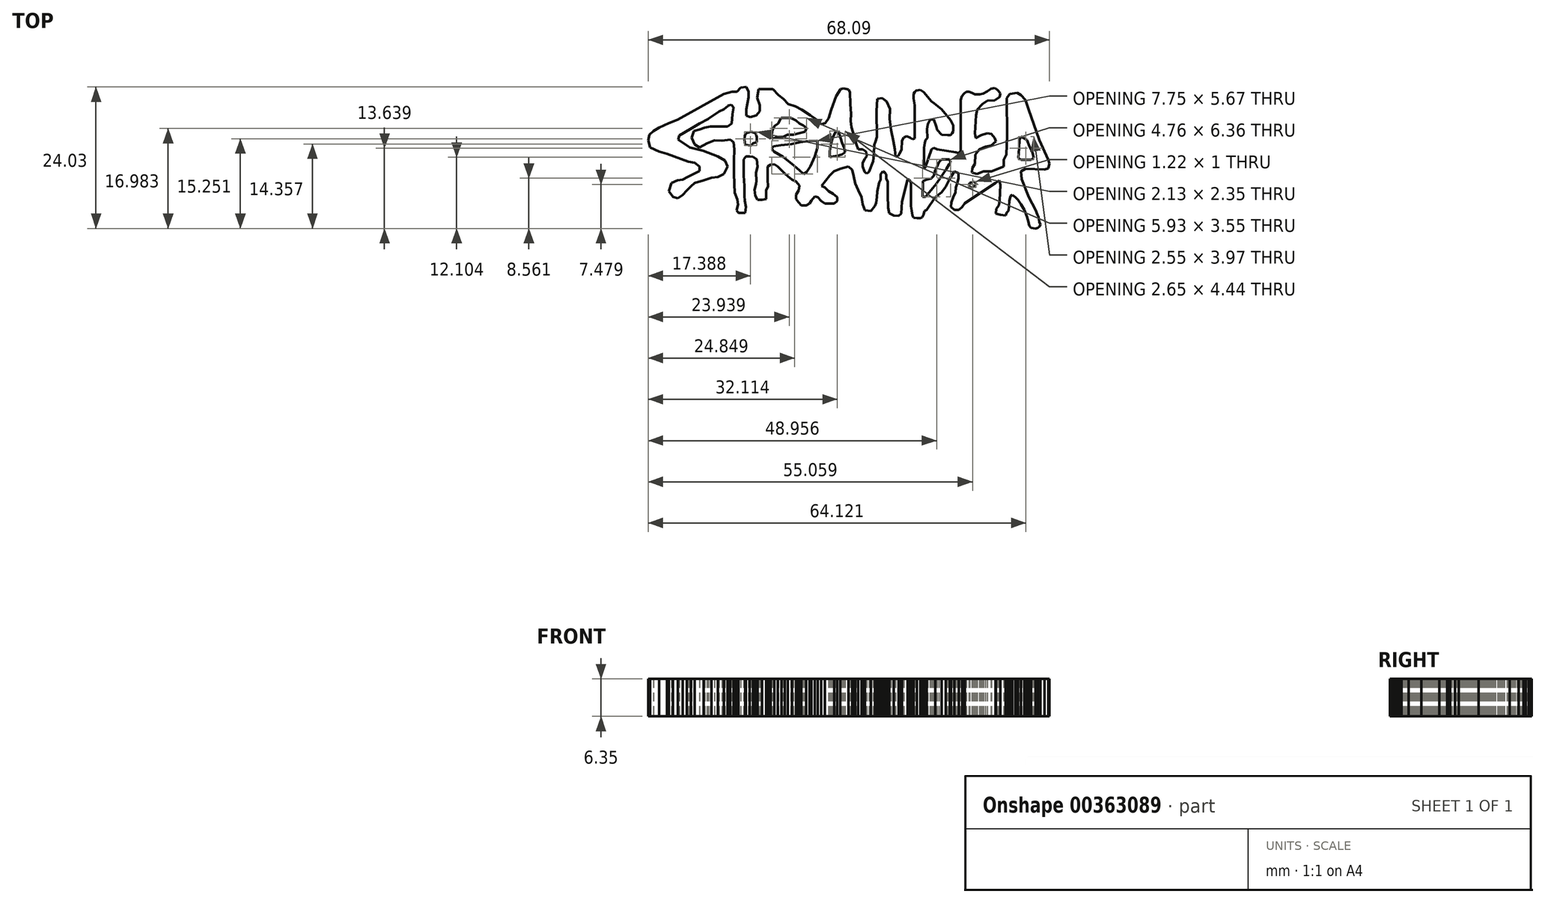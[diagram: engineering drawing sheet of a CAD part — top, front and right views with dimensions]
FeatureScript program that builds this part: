
annotation { "Feature Type Name" : "Feature", "Feature Type Description" : "" }
export const myFeature = defineFeature(function(context is Context, id is Id, definition is map)
    precondition{}
    {
        {
            var Q0;
            Q0=qCreatedBy(makeId("Top.planeOp"),FACE);
            var sketch = newSketch(context, id + "F0", { "sketchPlane" : qUnion([Q0])});
            skPoint(sketch, "E0", {"position": v(-28.93, -5.4) * mm});
            skPoint(sketch, "E1", {"position": v(-28.86, 4.62) * mm});
            skPoint(sketch, "E2", {"position": v(-19.82, 7.3) * mm});
            skPoint(sketch, "E3", {"position": v(-26.2, 6.07) * mm});
            skPoint(sketch, "E4", {"position": v(-26.62, 4.93) * mm});
            skPoint(sketch, "E5", {"position": v(-26.09, 3.8) * mm});
            skPoint(sketch, "E6", {"position": v(-25.23, 3.26) * mm});
            skPoint(sketch, "E7", {"position": v(-24.01, 3.96) * mm});
            skPoint(sketch, "E8", {"position": v(-22.75, 4.49) * mm});
            skPoint(sketch, "E9", {"position": v(-21.45, 4.4) * mm});
            skPoint(sketch, "E10", {"position": v(-20.02, 4.57) * mm});
            skPoint(sketch, "E11", {"position": v(-20.51, 0) * mm});
            skPoint(sketch, "E12", {"position": v(-20.92, 1.03) * mm});
            skPoint(sketch, "E13", {"position": v(-22.14, 1.76) * mm});
            skPoint(sketch, "E14", {"position": v(-24.62, 2.7) * mm});
            skPoint(sketch, "E15", {"position": v(-26.9, 3.26) * mm});
            skPoint(sketch, "E16", {"position": v(-26.82, 6.4) * mm});
            skPoint(sketch, "E17", {"position": v(-23.77, 8.1) * mm});
            skPoint(sketch, "E18", {"position": v(-21.94, 9.33) * mm});
            skPoint(sketch, "E19", {"position": v(-25.23, 7.33) * mm});
            skPoint(sketch, "E20", {"position": v(-28.12, -4.83) * mm});
            skPoint(sketch, "E21", {"position": v(-27.39, -4.02) * mm});
            skPoint(sketch, "E22", {"position": v(-26.74, -3.33) * mm});
            skPoint(sketch, "E23", {"position": v(-26.09, -2.76) * mm});
            skPoint(sketch, "E24", {"position": v(-24.54, -2.35) * mm});
            skPoint(sketch, "E25", {"position": v(-23.24, -1.9) * mm});
            skPoint(sketch, "E26", {"position": v(-22.14, -1.74) * mm});
            skPoint(sketch, "E27", {"position": v(-21.12, -1.25) * mm});
            skPoint(sketch, "E28", {"position": v(-29.79, -5.12) * mm});
            skPoint(sketch, "E29", {"position": v(-30.44, -4.18) * mm});
            skPoint(sketch, "E30", {"position": v(-30.03, -2.76) * mm});
            skPoint(sketch, "E31", {"position": v(-28.98, -2.31) * mm});
            skPoint(sketch, "E32", {"position": v(-28.12, -2.19) * mm});
            skPoint(sketch, "E33", {"position": v(-27.3, -1.74) * mm});
            skPoint(sketch, "E34", {"position": v(-26.09, -1.25) * mm});
            skPoint(sketch, "E35", {"position": v(-25.23, -0.76) * mm});
            skPoint(sketch, "E36", {"position": v(-25.23, 0) * mm});
            skPoint(sketch, "E37", {"position": v(-26.09, 0.66) * mm});
            skPoint(sketch, "E38", {"position": v(-27.18, 0.86) * mm});
            skPoint(sketch, "E39", {"position": v(-30.77, 2.17) * mm});
            skPoint(sketch, "E40", {"position": v(-32.1, 2.53) * mm});
            skPoint(sketch, "E41", {"position": v(-33.61, 3.26) * mm});
            skPoint(sketch, "E42", {"position": v(-33.98, 4.49) * mm});
            skPoint(sketch, "E43", {"position": v(-33.78, 5.42) * mm});
            skPoint(sketch, "E44", {"position": v(-21.12, 9.73) * mm});
            skPoint(sketch, "E45", {"position": v(-33.04, 6.07) * mm});
            skPoint(sketch, "E46", {"position": v(-32.1, 6.64) * mm});
            skPoint(sketch, "E47", {"position": v(-30.44, 7.37) * mm});
            skPoint(sketch, "E48", {"position": v(-29.02, 7.98) * mm});
            skPoint(sketch, "E49", {"position": v(-21.12, 12.34) * mm});
            skPoint(sketch, "E50", {"position": v(-19.74, 12.75) * mm});
            skPoint(sketch, "E51", {"position": v(-18.88, 12.75) * mm});
            skPoint(sketch, "E52", {"position": v(-18.27, 13.4) * mm});
            skPoint(sketch, "E53", {"position": v(-17.3, 13.52) * mm});
            skPoint(sketch, "E54", {"position": v(-16.97, 12.75) * mm});
            skPoint(sketch, "E55", {"position": v(-16.97, 11.77) * mm});
            skPoint(sketch, "E56", {"position": v(-17.3, 9.73) * mm});
            skPoint(sketch, "E57", {"position": v(-17.3, 8.68) * mm});
            skPoint(sketch, "E58", {"position": v(-16.6, 8.4) * mm});
            skPoint(sketch, "E59", {"position": v(-15.59, 8.72) * mm});
            skPoint(sketch, "E60", {"position": v(-15.02, 9.4) * mm});
            skPoint(sketch, "E61", {"position": v(-15.06, 10.43) * mm});
            skPoint(sketch, "E62", {"position": v(-15.5, 11.73) * mm});
            skPoint(sketch, "E63", {"position": v(-15.2, 13.17) * mm});
            skPoint(sketch, "E64", {"position": v(-12.8, 13.17) * mm});
            skPoint(sketch, "E65", {"position": v(-11.84, 12.14) * mm});
            skPoint(sketch, "E66", {"position": v(-11.03, 11.48) * mm});
            skPoint(sketch, "E67", {"position": v(-10.22, 10.63) * mm});
            skPoint(sketch, "E68", {"position": v(-9, 10.22) * mm});
            skPoint(sketch, "E69", {"position": v(-7.9, 9.65) * mm});
            skPoint(sketch, "E70", {"position": v(-6.47, 8.72) * mm});
            skPoint(sketch, "E71", {"position": v(-5.25, 7.9) * mm});
            skPoint(sketch, "E72", {"position": v(-4.64, 7.17) * mm});
            skPoint(sketch, "E73", {"position": v(-3.95, 7.37) * mm});
            skPoint(sketch, "E74", {"position": v(-3.38, 8.19) * mm});
            skPoint(sketch, "E75", {"position": v(-2.9, 9.65) * mm});
            skPoint(sketch, "E76", {"position": v(-2.08, 11.97) * mm});
            skPoint(sketch, "E77", {"position": v(-1.34, 13.17) * mm});
            skPoint(sketch, "E78", {"position": v(-24.38, 6.6) * mm});
            skPoint(sketch, "E79", {"position": v(-23.4, 6.8) * mm});
            skPoint(sketch, "E80", {"position": v(-22.26, 6.8) * mm});
            skPoint(sketch, "E81", {"position": v(-21.45, 6.8) * mm});
            skPoint(sketch, "E82", {"position": v(-20.47, 6.8) * mm});
            skPoint(sketch, "E83", {"position": v(-19.66, 8.88) * mm});
            skPoint(sketch, "E84", {"position": v(-17.66, 4.57) * mm});
            skPoint(sketch, "E85", {"position": v(-17.58, 5.25) * mm});
            skPoint(sketch, "E86", {"position": v(-17.4, 5.7) * mm});
            skPoint(sketch, "E87", {"position": v(-16.52, 5.92) * mm});
            skPoint(sketch, "E88", {"position": v(-25.23, 6.33) * mm});
            skPoint(sketch, "E89", {"position": v(-15.72, 5.7) * mm});
            skPoint(sketch, "E90", {"position": v(-15.53, 5) * mm});
            skPoint(sketch, "E91", {"position": v(-15.53, 4.17) * mm});
            skPoint(sketch, "E92", {"position": v(-16.2, 3.92) * mm});
            skPoint(sketch, "E93", {"position": v(-16.52, 3.56) * mm});
            skPoint(sketch, "E94", {"position": v(-17.52, 3.73) * mm});
            skPoint(sketch, "E95", {"position": v(-11.95, 7.33) * mm});
            skPoint(sketch, "E96", {"position": v(-12.56, 6.89) * mm});
            skPoint(sketch, "E97", {"position": v(-12.9, 6.17) * mm});
            skPoint(sketch, "E98", {"position": v(-13, 5.4) * mm});
            skPoint(sketch, "E99", {"position": v(-13, 4.7) * mm});
            skPoint(sketch, "E100", {"position": v(-11.95, 5) * mm});
            skPoint(sketch, "E101", {"position": v(-11.1, 5) * mm});
            skPoint(sketch, "E102", {"position": v(-10.32, 5.4) * mm});
            skPoint(sketch, "E103", {"position": v(-9.3, 5.4) * mm});
            skPoint(sketch, "E104", {"position": v(-8.35, 5.7) * mm});
            skPoint(sketch, "E105", {"position": v(-7.33, 5.92) * mm});
            skPoint(sketch, "E106", {"position": v(-7.08, 6.53) * mm});
            skPoint(sketch, "E107", {"position": v(-7.69, 7) * mm});
            skPoint(sketch, "E108", {"position": v(-8.32, 7.33) * mm});
            skPoint(sketch, "E109", {"position": v(-8.85, 7.8) * mm});
            skPoint(sketch, "E110", {"position": v(-11.4, 8.25) * mm});
            skPoint(sketch, "E111", {"position": v(-9.8, 8.25) * mm});
            skPoint(sketch, "E112", {"position": v(-19.45, 4.15) * mm});
            skPoint(sketch, "E113", {"position": v(-19.33, 2.97) * mm});
            skPoint(sketch, "E114", {"position": v(-19.41, 1.04) * mm});
            skPoint(sketch, "E115", {"position": v(-19.41, -1.12) * mm});
            skPoint(sketch, "E116", {"position": v(-19.33, -2.96) * mm});
            skPoint(sketch, "E117", {"position": v(-19.29, -4.43) * mm});
            skPoint(sketch, "E118", {"position": v(-18.84, -5.58) * mm});
            skPoint(sketch, "E119", {"position": v(-18.72, -6.44) * mm});
            skPoint(sketch, "E120", {"position": v(-18.96, -7.42) * mm});
            skPoint(sketch, "E121", {"position": v(-18.63, -7.87) * mm});
            skPoint(sketch, "E122", {"position": v(-17.53, -7.83) * mm});
            skPoint(sketch, "E123", {"position": v(-17.4, -6.85) * mm});
            skPoint(sketch, "E124", {"position": v(-17.57, -5.82) * mm});
            skPoint(sketch, "E125", {"position": v(-17.65, -4.93) * mm});
            skPoint(sketch, "E126", {"position": v(-17.61, -3.29) * mm});
            skPoint(sketch, "E127", {"position": v(-17.73, -1.53) * mm});
            skPoint(sketch, "E128", {"position": v(-17.73, 0) * mm});
            skPoint(sketch, "E129", {"position": v(-17.73, 1.25) * mm});
            skPoint(sketch, "E130", {"position": v(-17.4, 1.74) * mm});
            skPoint(sketch, "E131", {"position": v(-16.18, 1.66) * mm});
            skPoint(sketch, "E132", {"position": v(-15.53, 1.25) * mm});
            skPoint(sketch, "E133", {"position": v(-16.75, 1.74) * mm});
            skPoint(sketch, "E134", {"position": v(-15.44, 0) * mm});
            skPoint(sketch, "E135", {"position": v(-15.69, -1.04) * mm});
            skPoint(sketch, "E136", {"position": v(-15.6, -2.4) * mm});
            skPoint(sketch, "E137", {"position": v(-15.69, -2.96) * mm});
            skPoint(sketch, "E138", {"position": v(-15.4, -5.62) * mm});
            skPoint(sketch, "E139", {"position": v(-15.94, -3.94) * mm});
            skPoint(sketch, "E140", {"position": v(-15.81, -4.97) * mm});
            skPoint(sketch, "E141", {"position": v(-14.63, -5.66) * mm});
            skPoint(sketch, "E142", {"position": v(-13.97, -4.97) * mm});
            skPoint(sketch, "E143", {"position": v(-13.97, -5.5) * mm});
            skPoint(sketch, "E144", {"position": v(-13.97, -4.03) * mm});
            skPoint(sketch, "E145", {"position": v(-13.65, -3.33) * mm});
            skPoint(sketch, "E146", {"position": v(-13.69, -2.19) * mm});
            skPoint(sketch, "E147", {"position": v(-13.69, -0.96) * mm});
            skPoint(sketch, "E148", {"position": v(-13.69, 0) * mm});
            skPoint(sketch, "E149", {"position": v(-13.2, 0.35) * mm});
            skPoint(sketch, "E150", {"position": v(-12.54, 0.4) * mm});
            skPoint(sketch, "E151", {"position": v(-11.97, 0) * mm});
            skPoint(sketch, "E152", {"position": v(-11.36, -0.63) * mm});
            skPoint(sketch, "E153", {"position": v(-10.78, -1.16) * mm});
            skPoint(sketch, "E154", {"position": v(-10.25, -1.61) * mm});
            skPoint(sketch, "E155", {"position": v(-9.6, -2.19) * mm});
            skPoint(sketch, "E156", {"position": v(-8.9, -2.51) * mm});
            skPoint(sketch, "E157", {"position": v(-8.33, -3.2) * mm});
            skPoint(sketch, "E158", {"position": v(-8.45, -4.07) * mm});
            skPoint(sketch, "E159", {"position": v(-8.9, -4.76) * mm});
            skPoint(sketch, "E160", {"position": v(-8.9, -5.5) * mm});
            skPoint(sketch, "E161", {"position": v(-8.45, -6.07) * mm});
            skPoint(sketch, "E162", {"position": v(-8, -6.6) * mm});
            skPoint(sketch, "E163", {"position": v(-7.19, -6.6) * mm});
            skPoint(sketch, "E164", {"position": v(-6.61, -6.27) * mm});
            skPoint(sketch, "E165", {"position": v(-5.67, -5.09) * mm});
            skPoint(sketch, "E166", {"position": v(-5.18, -5.17) * mm});
            skPoint(sketch, "E167", {"position": v(-4, -6.27) * mm});
            skPoint(sketch, "E168", {"position": v(-3.34, -6.27) * mm});
            skPoint(sketch, "E169", {"position": v(-2.4, -6.27) * mm});
            skPoint(sketch, "E170", {"position": v(-1.87, -5.82) * mm});
            skPoint(sketch, "E171", {"position": v(-1.87, -5.17) * mm});
            skPoint(sketch, "E172", {"position": v(-2.6, -4.6) * mm});
            skPoint(sketch, "E173", {"position": v(-3.34, -4.15) * mm});
            skPoint(sketch, "E174", {"position": v(-4, -3.53) * mm});
            skPoint(sketch, "E175", {"position": v(-4.57, -3.29) * mm});
            skPoint(sketch, "E176", {"position": v(-3.14, -1.53) * mm});
            skPoint(sketch, "E177", {"position": v(-2.48, -0.8) * mm});
            skPoint(sketch, "E178", {"position": v(-1.38, -0.35) * mm});
            skPoint(sketch, "E179", {"position": v(0, 0) * mm});
            skPoint(sketch, "E180", {"position": v(0.62, -0.55) * mm});
            skPoint(sketch, "E181", {"position": v(-13, 3.03) * mm});
            skPoint(sketch, "E182", {"position": v(-12.62, 2.54) * mm});
            skPoint(sketch, "E183", {"position": v(-11.11, 1.64) * mm});
            skPoint(sketch, "E184", {"position": v(-9.55, 0.44) * mm});
            skPoint(sketch, "E185", {"position": v(-8.3, -0.65) * mm});
            skPoint(sketch, "E186", {"position": v(-7.58, -1.24) * mm});
            skPoint(sketch, "E187", {"position": v(-7.1, -0.95) * mm});
            skPoint(sketch, "E188", {"position": v(-6.48, 0) * mm});
            skPoint(sketch, "E189", {"position": v(-5.68, 1.72) * mm});
            skPoint(sketch, "E190", {"position": v(-5.28, 3.17) * mm});
            skPoint(sketch, "E191", {"position": v(-5.26, 4.43) * mm});
            skPoint(sketch, "E192", {"position": v(-6.7, 4.35) * mm});
            skPoint(sketch, "E193", {"position": v(-8.21, 4.16) * mm});
            skPoint(sketch, "E194", {"position": v(-9.62, 3.85) * mm});
            skPoint(sketch, "E195", {"position": v(-11.47, 3.63) * mm});
            skPoint(sketch, "E196", {"position": v(-12.71, 3.47) * mm});
            skPoint(sketch, "E197", {"position": v(-3.19, 1.63) * mm});
            skPoint(sketch, "E198", {"position": v(-1.83, 1.84) * mm});
            skPoint(sketch, "E199", {"position": v(-0.54, 2.43) * mm});
            skPoint(sketch, "E200", {"position": v(-1.06, 4.03) * mm});
            skPoint(sketch, "E201", {"position": v(-1.53, 5.47) * mm});
            skPoint(sketch, "E202", {"position": v(-2.08, 6.06) * mm});
            skPoint(sketch, "E203", {"position": v(-2.67, 4.94) * mm});
            skPoint(sketch, "E204", {"position": v(-3.06, 3.6) * mm});
            skPoint(sketch, "E205", {"position": v(-3.19, 2.54) * mm});
            skPoint(sketch, "E206", {"position": v(-2.87, 4.26) * mm});
            skPoint(sketch, "E207", {"position": v(-1.3, 4.83) * mm});
            skPoint(sketch, "E208", {"position": v(-0.69, 3.13) * mm});
            skPoint(sketch, "E209", {"position": v(-1.13, 2.02) * mm});
            skPoint(sketch, "E210", {"position": v(-2.5, 1.7) * mm});
            skPoint(sketch, "E211", {"position": v(-6.3, -5.73) * mm});
            skPoint(sketch, "E212", {"position": v(-4.6, -5.8) * mm});
            skPoint(sketch, "E213", {"position": v(0.92, -1.65) * mm});
            skPoint(sketch, "E214", {"position": v(1.2, -2.83) * mm});
            skPoint(sketch, "E215", {"position": v(1.69, -3.98) * mm});
            skPoint(sketch, "E216", {"position": v(2.26, -5.17) * mm});
            skPoint(sketch, "E217", {"position": v(2.41, -6.41) * mm});
            skPoint(sketch, "E218", {"position": v(2.78, -7.44) * mm});
            skPoint(sketch, "E219", {"position": v(3.82, -7.54) * mm});
            skPoint(sketch, "E220", {"position": v(4.5, -6.67) * mm});
            skPoint(sketch, "E221", {"position": v(4.88, -4.25) * mm});
            skPoint(sketch, "E222", {"position": v(4.84, -5.17) * mm});
            skPoint(sketch, "E223", {"position": v(5.21, -2.74) * mm});
            skPoint(sketch, "E224", {"position": v(5.47, -2.2) * mm});
            skPoint(sketch, "E225", {"position": v(5.45, -1.24) * mm});
            skPoint(sketch, "E226", {"position": v(5.85, -0.84) * mm});
            skPoint(sketch, "E227", {"position": v(6.19, -1) * mm});
            skPoint(sketch, "E228", {"position": v(6.43, -1.32) * mm});
            skPoint(sketch, "E229", {"position": v(6.43, -2.08) * mm});
            skPoint(sketch, "E230", {"position": v(6.65, -2.54) * mm});
            skPoint(sketch, "E231", {"position": v(6.67, -3.92) * mm});
            skPoint(sketch, "E232", {"position": v(6.67, -4.86) * mm});
            skPoint(sketch, "E233", {"position": v(4.75, -6.17) * mm});
            skPoint(sketch, "E234", {"position": v(6.73, -6.97) * mm});
            skPoint(sketch, "E235", {"position": v(6.94, -7.95) * mm});
            skPoint(sketch, "E236", {"position": v(7.72, -8.33) * mm});
            skPoint(sketch, "E237", {"position": v(8.5, -8.36) * mm});
            skPoint(sketch, "E238", {"position": v(8.94, -8.01) * mm});
            skPoint(sketch, "E239", {"position": v(9.1, -5.92) * mm});
            skPoint(sketch, "E240", {"position": v(10.07, -2.2) * mm});
            skPoint(sketch, "E241", {"position": v(10.35, -2.18) * mm});
            skPoint(sketch, "E242", {"position": v(10.6, -2.8) * mm});
            skPoint(sketch, "E243", {"position": v(10.6, -6.73) * mm});
            skPoint(sketch, "E244", {"position": v(10.74, -7.45) * mm});
            skPoint(sketch, "E245", {"position": v(10.9, -8.31) * mm});
            skPoint(sketch, "E246", {"position": v(11.07, -8.7) * mm});
            skPoint(sketch, "E247", {"position": v(12.2, -8.78) * mm});
            skPoint(sketch, "E248", {"position": v(12.54, -8.63) * mm});
            skPoint(sketch, "E249", {"position": v(12.78, -8.08) * mm});
            skPoint(sketch, "E250", {"position": v(13.3, -7.32) * mm});
            skPoint(sketch, "E251", {"position": v(12.93, -7.52) * mm});
            skPoint(sketch, "E252", {"position": v(-28.7, 5.3) * mm});
            skPoint(sketch, "E253", {"position": v(11.65, -8.73) * mm});
            skPoint(sketch, "E254", {"position": v(14.73, -5.17) * mm});
            skPoint(sketch, "E255", {"position": v(15.81, -4.37) * mm});
            skPoint(sketch, "E256", {"position": v(16.52, -3.42) * mm});
            skPoint(sketch, "E257", {"position": v(17.25, -2.02) * mm});
            skPoint(sketch, "E258", {"position": v(18, -0.84) * mm});
            skPoint(sketch, "E259", {"position": v(17.68, -1.32) * mm});
            skPoint(sketch, "E260", {"position": v(18.66, -1.1) * mm});
            skPoint(sketch, "E261", {"position": v(18.68, -1.94) * mm});
            skPoint(sketch, "E262", {"position": v(18.5, -2.8) * mm});
            skPoint(sketch, "E263", {"position": v(18.22, -3.53) * mm});
            skPoint(sketch, "E264", {"position": v(18.17, -4.37) * mm});
            skPoint(sketch, "E265", {"position": v(17.77, -5.17) * mm});
            skPoint(sketch, "E266", {"position": v(17.47, -6.1) * mm});
            skPoint(sketch, "E267", {"position": v(17.44, -6.83) * mm});
            skPoint(sketch, "E268", {"position": v(17.98, -7.32) * mm});
            skPoint(sketch, "E269", {"position": v(18.74, -7.32) * mm});
            skPoint(sketch, "E270", {"position": v(19.3, -6.83) * mm});
            skPoint(sketch, "E271", {"position": v(19.74, -6.18) * mm});
            skPoint(sketch, "E272", {"position": v(24.96, -2.8) * mm});
            skPoint(sketch, "E273", {"position": v(25.61, -2.34) * mm});
            skPoint(sketch, "E274", {"position": v(25.8, -3.13) * mm});
            skPoint(sketch, "E275", {"position": v(21.5, -3.26) * mm});
            skPoint(sketch, "E276", {"position": v(21.69, -2.8) * mm});
            skPoint(sketch, "E277", {"position": v(21.28, -2.53) * mm});
            skPoint(sketch, "E278", {"position": v(20.58, -2.8) * mm});
            skPoint(sketch, "E279", {"position": v(20.47, -3.2) * mm});
            skPoint(sketch, "E280", {"position": v(20.58, -3.48) * mm});
            skPoint(sketch, "E281", {"position": v(21.01, -3.53) * mm});
            skPoint(sketch, "E282", {"position": v(12.6, -5.13) * mm});
            skPoint(sketch, "E283", {"position": v(13.4, -4.78) * mm});
            skPoint(sketch, "E284", {"position": v(14.3, -3.64) * mm});
            skPoint(sketch, "E285", {"position": v(14.95, -2.94) * mm});
            skPoint(sketch, "E286", {"position": v(15.79, -1.7) * mm});
            skPoint(sketch, "E287", {"position": v(16.68, -0.34) * mm});
            skPoint(sketch, "E288", {"position": v(17.11, 0.37) * mm});
            skPoint(sketch, "E289", {"position": v(17.36, 0.7) * mm});
            skPoint(sketch, "E290", {"position": v(16.55, 1.23) * mm});
            skPoint(sketch, "E291", {"position": v(17.14, 1.23) * mm});
            skPoint(sketch, "E292", {"position": v(15.81, 1.23) * mm});
            skPoint(sketch, "E293", {"position": v(15.38, 0.77) * mm});
            skPoint(sketch, "E294", {"position": v(15.06, 0) * mm});
            skPoint(sketch, "E295", {"position": v(14.73, -0.6) * mm});
            skPoint(sketch, "E296", {"position": v(14.49, -1.56) * mm});
            skPoint(sketch, "E297", {"position": v(14.06, -1.99) * mm});
            skPoint(sketch, "E298", {"position": v(13.3, -2.2) * mm});
            skPoint(sketch, "E299", {"position": v(12.65, -2.45) * mm});
            skPoint(sketch, "E300", {"position": v(12.65, -2.9) * mm});
            skPoint(sketch, "E301", {"position": v(13.1, -5.1) * mm});
            skPoint(sketch, "E302", {"position": v(25.66, -5.78) * mm});
            skPoint(sketch, "E303", {"position": v(25.53, -6.58) * mm});
            skPoint(sketch, "E304", {"position": v(25.12, -7.16) * mm});
            skPoint(sketch, "E305", {"position": v(25.06, -7.98) * mm});
            skPoint(sketch, "E306", {"position": v(25.8, -8.2) * mm});
            skPoint(sketch, "E307", {"position": v(26.7, -8.3) * mm});
            skPoint(sketch, "E308", {"position": v(26.89, -7.78) * mm});
            skPoint(sketch, "E309", {"position": v(27.18, -7.5) * mm});
            skPoint(sketch, "E310", {"position": v(27.27, -6.7) * mm});
            skPoint(sketch, "E311", {"position": v(27.32, -5.8) * mm});
            skPoint(sketch, "E312", {"position": v(27.48, -5.01) * mm});
            skPoint(sketch, "E313", {"position": v(27.8, -4.84) * mm});
            skPoint(sketch, "E314", {"position": v(28.34, -5.17) * mm});
            skPoint(sketch, "E315", {"position": v(28.78, -5.64) * mm});
            skPoint(sketch, "E316", {"position": v(29.28, -6.41) * mm});
            skPoint(sketch, "E317", {"position": v(29.83, -7.36) * mm});
            skPoint(sketch, "E318", {"position": v(30.27, -8.48) * mm});
            skPoint(sketch, "E319", {"position": v(30.54, -9.37) * mm});
            skPoint(sketch, "E320", {"position": v(30.7, -10.01) * mm});
            skPoint(sketch, "E321", {"position": v(31, -10.38) * mm});
            skPoint(sketch, "E322", {"position": v(31.73, -10.5) * mm});
            skPoint(sketch, "E323", {"position": v(32.16, -10.37) * mm});
            skPoint(sketch, "E324", {"position": v(32.45, -10.17) * mm});
            skPoint(sketch, "E325", {"position": v(32.57, -9.81) * mm});
            skPoint(sketch, "E326", {"position": v(32.34, -8.94) * mm});
            skPoint(sketch, "E327", {"position": v(32.4, -9.37) * mm});
            skPoint(sketch, "E328", {"position": v(32.1, -8.2) * mm});
            skPoint(sketch, "E329", {"position": v(32.25, -8.53) * mm});
            skPoint(sketch, "E330", {"position": v(31.75, -7.34) * mm});
            skPoint(sketch, "E331", {"position": v(30.6, -5.17) * mm});
            skPoint(sketch, "E332", {"position": v(29.42, -2.12) * mm});
            skPoint(sketch, "E333", {"position": v(29.28, -0.82) * mm});
            skPoint(sketch, "E334", {"position": v(30.02, -0.36) * mm});
            skPoint(sketch, "E335", {"position": v(33.28, -0.5) * mm});
            skPoint(sketch, "E336", {"position": v(33.92, -0.3) * mm});
            skPoint(sketch, "E337", {"position": v(34.11, 0.52) * mm});
            skPoint(sketch, "E338", {"position": v(33.92, 1.15) * mm});
            skPoint(sketch, "E339", {"position": v(32.42, 4.53) * mm});
            skPoint(sketch, "E340", {"position": v(30.54, 9.81) * mm});
            skPoint(sketch, "E341", {"position": v(30.07, 11.31) * mm});
            skPoint(sketch, "E342", {"position": v(29.28, 12.14) * mm});
            skPoint(sketch, "E343", {"position": v(28.67, 12.51) * mm});
            skPoint(sketch, "E344", {"position": v(27.37, 12.31) * mm});
            skPoint(sketch, "E345", {"position": v(26.87, 11.64) * mm});
            skPoint(sketch, "E346", {"position": v(26.92, 5.31) * mm});
            skPoint(sketch, "E347", {"position": v(26.84, 2.06) * mm});
            skPoint(sketch, "E348", {"position": v(26.4, 1.15) * mm});
            skPoint(sketch, "E349", {"position": v(26.37, 0) * mm});
            skPoint(sketch, "E350", {"position": v(29.28, 5.11) * mm});
            skPoint(sketch, "E351", {"position": v(30.3, 4.53) * mm});
            skPoint(sketch, "E352", {"position": v(30.77, 3.41) * mm});
            skPoint(sketch, "E353", {"position": v(31.24, 2.36) * mm});
            skPoint(sketch, "E354", {"position": v(31.42, 1.46) * mm});
            skPoint(sketch, "E355", {"position": v(31.02, 1.15) * mm});
            skPoint(sketch, "E356", {"position": v(30.3, 1.15) * mm});
            skPoint(sketch, "E357", {"position": v(29.28, 1.15) * mm});
            skPoint(sketch, "E358", {"position": v(28.87, 1.46) * mm});
            skPoint(sketch, "E359", {"position": v(28.97, 3.14) * mm});
            skPoint(sketch, "E360", {"position": v(29.07, 4.53) * mm});
            skPoint(sketch, "E361", {"position": v(24.28, -0.84) * mm});
            skPoint(sketch, "E362", {"position": v(22.96, -0.84) * mm});
            skPoint(sketch, "E363", {"position": v(21.82, -1.24) * mm});
            skPoint(sketch, "E364", {"position": v(20.97, -1.02) * mm});
            skPoint(sketch, "E365", {"position": v(21.04, -0.23) * mm});
            skPoint(sketch, "E366", {"position": v(21.5, 0.46) * mm});
            skPoint(sketch, "E367", {"position": v(21.57, 2.06) * mm});
            skPoint(sketch, "E368", {"position": v(22.26, 2.9) * mm});
            skPoint(sketch, "E369", {"position": v(23.24, 3.41) * mm});
            skPoint(sketch, "E370", {"position": v(24.18, 3.6) * mm});
            skPoint(sketch, "E371", {"position": v(25.03, 4.26) * mm});
            skPoint(sketch, "E372", {"position": v(24.81, 4.83) * mm});
            skPoint(sketch, "E373", {"position": v(24.28, 5.56) * mm});
            skPoint(sketch, "E374", {"position": v(23.59, 5.69) * mm});
            skPoint(sketch, "E375", {"position": v(22.58, 5.37) * mm});
            skPoint(sketch, "E376", {"position": v(21.63, 4.83) * mm});
            skPoint(sketch, "E377", {"position": v(21.5, 5.69) * mm});
            skPoint(sketch, "E378", {"position": v(21.65, 8.7) * mm});
            skPoint(sketch, "E379", {"position": v(21.86, 9.66) * mm});
            skPoint(sketch, "E380", {"position": v(22.73, 10.65) * mm});
            skPoint(sketch, "E381", {"position": v(23.59, 11.18) * mm});
            skPoint(sketch, "E382", {"position": v(24.81, 11.28) * mm});
            skPoint(sketch, "E383", {"position": v(25.67, 11.82) * mm});
            skPoint(sketch, "E384", {"position": v(25.8, 12.43) * mm});
            skPoint(sketch, "E385", {"position": v(25.28, 13.02) * mm});
            skPoint(sketch, "E386", {"position": v(24.81, 13.36) * mm});
            skPoint(sketch, "E387", {"position": v(24.18, 13.22) * mm});
            skPoint(sketch, "E388", {"position": v(23.59, 12.8) * mm});
            skPoint(sketch, "E389", {"position": v(22.89, 12.39) * mm});
            skPoint(sketch, "E390", {"position": v(22.3, 12.25) * mm});
            skPoint(sketch, "E391", {"position": v(21.5, 12.28) * mm});
            skPoint(sketch, "E392", {"position": v(20.95, 12.55) * mm});
            skPoint(sketch, "E393", {"position": v(20.47, 12.7) * mm});
            skPoint(sketch, "E394", {"position": v(20.03, 12.69) * mm});
            skPoint(sketch, "E395", {"position": v(19.66, 12.4) * mm});
            skPoint(sketch, "E396", {"position": v(19.25, 11.95) * mm});
            skPoint(sketch, "E397", {"position": v(19.06, 11.32) * mm});
            skPoint(sketch, "E398", {"position": v(19.06, 10.44) * mm});
            skPoint(sketch, "E399", {"position": v(19.06, 2.66) * mm});
            skPoint(sketch, "E400", {"position": v(18.68, 2.32) * mm});
            skPoint(sketch, "E401", {"position": v(18.26, 2.43) * mm});
            skPoint(sketch, "E402", {"position": v(15.08, 2.9) * mm});
            skPoint(sketch, "E403", {"position": v(14.47, 3.19) * mm});
            skPoint(sketch, "E404", {"position": v(14.1, 2.9) * mm});
            skPoint(sketch, "E405", {"position": v(13, -0.2) * mm});
            skPoint(sketch, "E406", {"position": v(12.86, -0.45) * mm});
            skPoint(sketch, "E407", {"position": v(12.86, 3.19) * mm});
            skPoint(sketch, "E408", {"position": v(12.96, 4.01) * mm});
            skPoint(sketch, "E409", {"position": v(13.12, 4.53) * mm});
            skPoint(sketch, "E410", {"position": v(13.41, 4.83) * mm});
            skPoint(sketch, "E411", {"position": v(13.38, 6.4) * mm});
            skPoint(sketch, "E412", {"position": v(13.48, 7.18) * mm});
            skPoint(sketch, "E413", {"position": v(13.83, 7.94) * mm});
            skPoint(sketch, "E414", {"position": v(14.47, 8.05) * mm});
            skPoint(sketch, "E415", {"position": v(14.91, 6.76) * mm});
            skPoint(sketch, "E416", {"position": v(15.06, 6.22) * mm});
            skPoint(sketch, "E417", {"position": v(15.81, 5.43) * mm});
            skPoint(sketch, "E418", {"position": v(16.81, 5.37) * mm});
            skPoint(sketch, "E419", {"position": v(17.36, 5.37) * mm});
            skPoint(sketch, "E420", {"position": v(17.77, 6.01) * mm});
            skPoint(sketch, "E421", {"position": v(17.77, 7.02) * mm});
            skPoint(sketch, "E422", {"position": v(17.62, 5.68) * mm});
            skPoint(sketch, "E423", {"position": v(17.47, 7.62) * mm});
            skPoint(sketch, "E424", {"position": v(15.8, 9.71) * mm});
            skPoint(sketch, "E425", {"position": v(14.58, 10.72) * mm});
            skPoint(sketch, "E426", {"position": v(14.1, 11.04) * mm});
            skPoint(sketch, "E427", {"position": v(12.78, 12.64) * mm});
            skPoint(sketch, "E428", {"position": v(12.2, 13) * mm});
            skPoint(sketch, "E429", {"position": v(11.53, 12.89) * mm});
            skPoint(sketch, "E430", {"position": v(11.05, 12.32) * mm});
            skPoint(sketch, "E431", {"position": v(11.23, 12.64) * mm});
            skPoint(sketch, "E432", {"position": v(11.05, 11.57) * mm});
            skPoint(sketch, "E433", {"position": v(11.23, 10.4) * mm});
            skPoint(sketch, "E434", {"position": v(11.23, 5.8) * mm});
            skPoint(sketch, "E435", {"position": v(11.23, 4.79) * mm});
            skPoint(sketch, "E436", {"position": v(10.9, 4.66) * mm});
            skPoint(sketch, "E437", {"position": v(10.52, 4.93) * mm});
            skPoint(sketch, "E438", {"position": v(9.92, 5.17) * mm});
            skPoint(sketch, "E439", {"position": v(9.4, 4.97) * mm});
            skPoint(sketch, "E440", {"position": v(9.07, 4.43) * mm});
            skPoint(sketch, "E441", {"position": v(9.03, 2.86) * mm});
            skPoint(sketch, "E442", {"position": v(8.68, 2.15) * mm});
            skPoint(sketch, "E443", {"position": v(8.48, 1.78) * mm});
            skPoint(sketch, "E444", {"position": v(8.05, 1.69) * mm});
            skPoint(sketch, "E445", {"position": v(7.89, 2.93) * mm});
            skPoint(sketch, "E446", {"position": v(7.66, 4.31) * mm});
            skPoint(sketch, "E447", {"position": v(7.28, 6.17) * mm});
            skPoint(sketch, "E448", {"position": v(7.02, 8.07) * mm});
            skPoint(sketch, "E449", {"position": v(7.04, 9.77) * mm});
            skPoint(sketch, "E450", {"position": v(6.5, 11.06) * mm});
            skPoint(sketch, "E451", {"position": v(5.75, 11.63) * mm});
            skPoint(sketch, "E452", {"position": v(4.88, 11.52) * mm});
            skPoint(sketch, "E453", {"position": v(4.77, 9.44) * mm});
            skPoint(sketch, "E454", {"position": v(4.81, 5) * mm});
            skPoint(sketch, "E455", {"position": v(4.42, 3.72) * mm});
            skPoint(sketch, "E456", {"position": v(4.57, 4.18) * mm});
            skPoint(sketch, "E457", {"position": v(4.3, 2.1) * mm});
            skPoint(sketch, "E458", {"position": v(4.22, 0.88) * mm});
            skPoint(sketch, "E459", {"position": v(3.48, -0.84) * mm});
            skPoint(sketch, "E460", {"position": v(3.13, -1.21) * mm});
            skPoint(sketch, "E461", {"position": v(2.74, -0.84) * mm});
            skPoint(sketch, "E462", {"position": v(2.43, 0) * mm});
            skPoint(sketch, "E463", {"position": v(2.4, 0.64) * mm});
            skPoint(sketch, "E464", {"position": v(2.82, 1.34) * mm});
            skPoint(sketch, "E465", {"position": v(3.1, 1.82) * mm});
            skPoint(sketch, "E466", {"position": v(3.02, 2.56) * mm});
            skPoint(sketch, "E467", {"position": v(2.45, 2.93) * mm});
            skPoint(sketch, "E468", {"position": v(1.67, 2.93) * mm});
            skPoint(sketch, "E469", {"position": v(1.32, 3.83) * mm});
            skPoint(sketch, "E470", {"position": v(0.95, 5.23) * mm});
            skPoint(sketch, "E471", {"position": v(0.53, 6.7) * mm});
            skPoint(sketch, "E472", {"position": v(0.4, 7.78) * mm});
            skPoint(sketch, "E473", {"position": v(0.49, 8.94) * mm});
            skPoint(sketch, "E474", {"position": v(0.33, 10.6) * mm});
            skPoint(sketch, "E475", {"position": v(0.3, 12.66) * mm});
            skPoint(sketch, "E476", {"position": v(0, 13.09) * mm});
            skLineSegment(sketch, "E477", {"start": v(-30.03, -2.76) * mm, "end": v(-30.44, -4.18) * mm});
            skLineSegment(sketch, "E478", {"start": v(-30.44, -4.18) * mm, "end": v(-29.79, -5.12) * mm});
            skLineSegment(sketch, "E479", {"start": v(-29.76, -5.12) * mm, "end": v(-28.93, -5.4) * mm});
            skLineSegment(sketch, "E480", {"start": v(-28.93, -5.4) * mm, "end": v(-28.12, -4.83) * mm});
            skLineSegment(sketch, "E481", {"start": v(-28.12, -4.83) * mm, "end": v(-27.39, -4.02) * mm});
            skLineSegment(sketch, "E482", {"start": v(-27.39, -4.02) * mm, "end": v(-26.74, -3.33) * mm});
            skLineSegment(sketch, "E483", {"start": v(-26.74, -3.33) * mm, "end": v(-26.09, -2.76) * mm});
            skLineSegment(sketch, "E484", {"start": v(-26.09, -2.76) * mm, "end": v(-24.54, -2.35) * mm});
            skLineSegment(sketch, "E485", {"start": v(-24.54, -2.35) * mm, "end": v(-23.24, -1.9) * mm});
            skLineSegment(sketch, "E486", {"start": v(-23.24, -1.9) * mm, "end": v(-22.14, -1.74) * mm});
            skLineSegment(sketch, "E487", {"start": v(-22.14, -1.74) * mm, "end": v(-21.12, -1.25) * mm});
            skLineSegment(sketch, "E488", {"start": v(-21.12, -1.25) * mm, "end": v(-20.51, 0) * mm});
            skLineSegment(sketch, "E489", {"start": v(-20.51, 0) * mm, "end": v(-20.92, 1.03) * mm});
            skLineSegment(sketch, "E490", {"start": v(-20.92, 1.03) * mm, "end": v(-22.14, 1.76) * mm});
            skLineSegment(sketch, "E491", {"start": v(-22.14, 1.76) * mm, "end": v(-24.62, 2.7) * mm});
            skLineSegment(sketch, "E492", {"start": v(-24.62, 2.7) * mm, "end": v(-26.9, 3.26) * mm});
            skLineSegment(sketch, "E493", {"start": v(-26.9, 3.26) * mm, "end": v(-28.86, 4.62) * mm});
            skLineSegment(sketch, "E494", {"start": v(-28.86, 4.62) * mm, "end": v(-28.7, 5.3) * mm});
            skLineSegment(sketch, "E495", {"start": v(-28.7, 5.3) * mm, "end": v(-26.82, 6.4) * mm});
            skLineSegment(sketch, "E496", {"start": v(-26.82, 6.4) * mm, "end": v(-25.23, 7.33) * mm});
            skLineSegment(sketch, "E497", {"start": v(-25.23, 7.33) * mm, "end": v(-23.77, 8.1) * mm});
            skLineSegment(sketch, "E498", {"start": v(-23.75, 8.11) * mm, "end": v(-21.94, 9.33) * mm});
            skLineSegment(sketch, "E499", {"start": v(-21.94, 9.33) * mm, "end": v(-21.12, 9.73) * mm});
            skLineSegment(sketch, "E500", {"start": v(-19.66, 8.88) * mm, "end": v(-19.82, 7.3) * mm});
            skLineSegment(sketch, "E501", {"start": v(-19.82, 7.3) * mm, "end": v(-20.47, 6.8) * mm});
            skLineSegment(sketch, "E502", {"start": v(-20.47, 6.8) * mm, "end": v(-21.45, 6.8) * mm});
            skPoint(sketch, "E503", {"position": v(-20.42, 10.31) * mm});
            skPoint(sketch, "E504", {"position": v(-19.85, 10.52) * mm});
            skPoint(sketch, "E505", {"position": v(-19.47, 10.02) * mm});
            skLineSegment(sketch, "E506", {"start": v(-21.12, 9.73) * mm, "end": v(-20.42, 10.31) * mm});
            skLineSegment(sketch, "E507", {"start": v(-20.42, 10.36) * mm, "end": v(-19.85, 10.52) * mm});
            skLineSegment(sketch, "E508", {"start": v(-19.85, 10.52) * mm, "end": v(-19.47, 10.02) * mm});
            skLineSegment(sketch, "E509", {"start": v(-19.47, 10.02) * mm, "end": v(-19.66, 8.88) * mm});
            skLineSegment(sketch, "E510", {"start": v(-21.45, 6.8) * mm, "end": v(-22.26, 6.8) * mm});
            skLineSegment(sketch, "E511", {"start": v(-22.26, 6.8) * mm, "end": v(-23.4, 6.8) * mm});
            skLineSegment(sketch, "E512", {"start": v(-23.4, 6.8) * mm, "end": v(-24.38, 6.6) * mm});
            skLineSegment(sketch, "E513", {"start": v(-24.38, 6.6) * mm, "end": v(-25.23, 6.33) * mm});
            skLineSegment(sketch, "E514", {"start": v(-25.23, 6.33) * mm, "end": v(-26.2, 6.07) * mm});
            skLineSegment(sketch, "E515", {"start": v(-26.2, 6.07) * mm, "end": v(-26.62, 4.93) * mm});
            skLineSegment(sketch, "E516", {"start": v(-26.62, 4.93) * mm, "end": v(-26.09, 3.8) * mm});
            skLineSegment(sketch, "E517", {"start": v(-26.09, 3.8) * mm, "end": v(-25.23, 3.26) * mm});
            skLineSegment(sketch, "E518", {"start": v(-25.23, 3.26) * mm, "end": v(-24.01, 3.96) * mm});
            skLineSegment(sketch, "E519", {"start": v(-24.01, 3.96) * mm, "end": v(-22.75, 4.49) * mm});
            skLineSegment(sketch, "E520", {"start": v(-22.75, 4.49) * mm, "end": v(-21.45, 4.4) * mm});
            skLineSegment(sketch, "E521", {"start": v(-21.45, 4.4) * mm, "end": v(-20.02, 4.57) * mm});
            skLineSegment(sketch, "E522", {"start": v(-20.02, 4.57) * mm, "end": v(-19.45, 4.15) * mm});
            skLineSegment(sketch, "E523", {"start": v(-19.45, 4.15) * mm, "end": v(-19.33, 2.97) * mm});
            skLineSegment(sketch, "E524", {"start": v(-19.33, 2.97) * mm, "end": v(-19.41, 1.04) * mm});
            skLineSegment(sketch, "E525", {"start": v(-19.41, 1.04) * mm, "end": v(-19.41, -1.12) * mm});
            skLineSegment(sketch, "E526", {"start": v(-19.41, -1.12) * mm, "end": v(-19.33, -2.96) * mm});
            skLineSegment(sketch, "E527", {"start": v(-19.33, -2.96) * mm, "end": v(-19.29, -4.43) * mm});
            skLineSegment(sketch, "E528", {"start": v(-19.29, -4.43) * mm, "end": v(-18.84, -5.58) * mm});
            skLineSegment(sketch, "E529", {"start": v(-18.84, -5.58) * mm, "end": v(-18.72, -6.44) * mm});
            skLineSegment(sketch, "E530", {"start": v(-18.72, -6.44) * mm, "end": v(-18.96, -7.42) * mm});
            skLineSegment(sketch, "E531", {"start": v(-18.96, -7.42) * mm, "end": v(-18.63, -7.87) * mm});
            skLineSegment(sketch, "E532", {"start": v(-18.63, -7.87) * mm, "end": v(-17.53, -7.83) * mm});
            skLineSegment(sketch, "E533", {"start": v(-17.53, -7.83) * mm, "end": v(-17.4, -6.85) * mm});
            skLineSegment(sketch, "E534", {"start": v(-17.4, -6.85) * mm, "end": v(-17.57, -5.82) * mm});
            skLineSegment(sketch, "E535", {"start": v(-17.57, -5.82) * mm, "end": v(-17.65, -4.93) * mm});
            skLineSegment(sketch, "E536", {"start": v(-17.65, -4.93) * mm, "end": v(-17.61, -3.29) * mm});
            skLineSegment(sketch, "E537", {"start": v(-17.61, -3.29) * mm, "end": v(-17.73, -1.53) * mm});
            skLineSegment(sketch, "E538", {"start": v(-17.73, -1.53) * mm, "end": v(-17.73, 0) * mm});
            skLineSegment(sketch, "E539", {"start": v(-17.73, 0) * mm, "end": v(-17.73, 1.25) * mm});
            skLineSegment(sketch, "E540", {"start": v(-17.73, 1.25) * mm, "end": v(-17.4, 1.74) * mm});
            skLineSegment(sketch, "E541", {"start": v(-17.4, 1.74) * mm, "end": v(-16.75, 1.74) * mm});
            skLineSegment(sketch, "E542", {"start": v(-16.75, 1.74) * mm, "end": v(-16.18, 1.66) * mm});
            skLineSegment(sketch, "E543", {"start": v(-17.52, 3.73) * mm, "end": v(-17.66, 4.57) * mm});
            skLineSegment(sketch, "E544", {"start": v(-17.66, 4.57) * mm, "end": v(-17.58, 5.25) * mm});
            skLineSegment(sketch, "E545", {"start": v(-17.58, 5.25) * mm, "end": v(-17.4, 5.7) * mm});
            skLineSegment(sketch, "E546", {"start": v(-29.76, -5.12) * mm, "end": v(-29.79, -5.12) * mm});
            skLineSegment(sketch, "E547", {"start": v(-23.77, 8.1) * mm, "end": v(-23.75, 8.11) * mm});
            skLineSegment(sketch, "E548", {"start": v(-20.42, 10.31) * mm, "end": v(-20.42, 10.36) * mm});
            skLineSegment(sketch, "E549", {"start": v(-16.52, 3.56) * mm, "end": v(-16.2, 3.92) * mm});
            skLineSegment(sketch, "E550", {"start": v(-16.2, 3.92) * mm, "end": v(-15.53, 4.17) * mm});
            skLineSegment(sketch, "E551", {"start": v(-17.4, 5.7) * mm, "end": v(-16.52, 5.92) * mm});
            skLineSegment(sketch, "E552", {"start": v(-16.52, 5.92) * mm, "end": v(-15.72, 5.7) * mm});
            skLineSegment(sketch, "E553", {"start": v(-15.72, 5.7) * mm, "end": v(-15.53, 5) * mm});
            skLineSegment(sketch, "E554", {"start": v(-15.53, 5) * mm, "end": v(-15.53, 4.17) * mm});
            skLineSegment(sketch, "E555", {"start": v(-16.18, 1.66) * mm, "end": v(-15.53, 1.25) * mm});
            skLineSegment(sketch, "E556", {"start": v(-15.53, 1.25) * mm, "end": v(-15.44, 0) * mm});
            skLineSegment(sketch, "E557", {"start": v(-15.44, 0) * mm, "end": v(-15.69, -1.04) * mm});
            skLineSegment(sketch, "E558", {"start": v(-15.69, -1.04) * mm, "end": v(-15.6, -2.4) * mm});
            skLineSegment(sketch, "E559", {"start": v(-15.6, -2.4) * mm, "end": v(-15.69, -2.96) * mm});
            skLineSegment(sketch, "E560", {"start": v(-15.69, -2.96) * mm, "end": v(-15.94, -3.94) * mm});
            skLineSegment(sketch, "E561", {"start": v(-15.94, -3.94) * mm, "end": v(-15.81, -4.97) * mm});
            skLineSegment(sketch, "E562", {"start": v(-15.81, -4.97) * mm, "end": v(-15.4, -5.62) * mm});
            skLineSegment(sketch, "E563", {"start": v(-15.4, -5.62) * mm, "end": v(-14.63, -5.66) * mm});
            skLineSegment(sketch, "E564", {"start": v(-14.63, -5.66) * mm, "end": v(-13.97, -5.5) * mm});
            skLineSegment(sketch, "E565", {"start": v(-13.97, -5.5) * mm, "end": v(-13.97, -4.97) * mm});
            skLineSegment(sketch, "E566", {"start": v(-13.97, -4.97) * mm, "end": v(-13.97, -4.03) * mm});
            skLineSegment(sketch, "E567", {"start": v(-13.97, -4.03) * mm, "end": v(-13.65, -3.33) * mm});
            skLineSegment(sketch, "E568", {"start": v(-13.65, -3.33) * mm, "end": v(-13.69, -2.19) * mm});
            skLineSegment(sketch, "E569", {"start": v(-13.69, -2.19) * mm, "end": v(-13.69, -0.96) * mm});
            skLineSegment(sketch, "E570", {"start": v(-13.69, -0.96) * mm, "end": v(-13.69, 0) * mm});
            skLineSegment(sketch, "E571", {"start": v(-13.69, 0) * mm, "end": v(-13.2, 0.35) * mm});
            skLineSegment(sketch, "E572", {"start": v(-13.2, 0.35) * mm, "end": v(-12.54, 0.4) * mm});
            skLineSegment(sketch, "E573", {"start": v(-12.54, 0.4) * mm, "end": v(-11.97, 0) * mm});
            skLineSegment(sketch, "E574", {"start": v(-11.97, 0) * mm, "end": v(-11.36, -0.63) * mm});
            skLineSegment(sketch, "E575", {"start": v(-11.36, -0.63) * mm, "end": v(-10.78, -1.16) * mm});
            skLineSegment(sketch, "E576", {"start": v(-10.78, -1.16) * mm, "end": v(-10.25, -1.61) * mm});
            skLineSegment(sketch, "E577", {"start": v(-10.25, -1.61) * mm, "end": v(-9.6, -2.19) * mm});
            skLineSegment(sketch, "E578", {"start": v(-9.6, -2.19) * mm, "end": v(-8.9, -2.51) * mm});
            skLineSegment(sketch, "E579", {"start": v(-8.9, -2.51) * mm, "end": v(-8.33, -3.2) * mm});
            skLineSegment(sketch, "E580", {"start": v(-13, 4.7) * mm, "end": v(-11.95, 5) * mm});
            skLineSegment(sketch, "E581", {"start": v(-13, 4.7) * mm, "end": v(-13, 5.4) * mm});
            skLineSegment(sketch, "E582", {"start": v(-13, 5.4) * mm, "end": v(-12.9, 6.17) * mm});
            skLineSegment(sketch, "E583", {"start": v(-12.9, 6.17) * mm, "end": v(-12.56, 6.89) * mm});
            skLineSegment(sketch, "E584", {"start": v(-12.56, 6.89) * mm, "end": v(-11.95, 7.33) * mm});
            skLineSegment(sketch, "E585", {"start": v(-8.85, 7.8) * mm, "end": v(-8.32, 7.33) * mm});
            skLineSegment(sketch, "E586", {"start": v(-8.32, 7.33) * mm, "end": v(-7.69, 7) * mm});
            skLineSegment(sketch, "E587", {"start": v(-7.69, 7) * mm, "end": v(-7.08, 6.53) * mm});
            skLineSegment(sketch, "E588", {"start": v(-7.08, 6.53) * mm, "end": v(-7.33, 5.92) * mm});
            skLineSegment(sketch, "E589", {"start": v(-7.33, 5.92) * mm, "end": v(-8.35, 5.7) * mm});
            skLineSegment(sketch, "E590", {"start": v(-8.35, 5.7) * mm, "end": v(-9.3, 5.4) * mm});
            skLineSegment(sketch, "E591", {"start": v(-9.3, 5.4) * mm, "end": v(-10.32, 5.4) * mm});
            skLineSegment(sketch, "E592", {"start": v(-10.32, 5.4) * mm, "end": v(-11.1, 5) * mm});
            skLineSegment(sketch, "E593", {"start": v(-11.1, 5) * mm, "end": v(-11.95, 5) * mm});
            skLineSegment(sketch, "E594", {"start": v(-12.62, 2.54) * mm, "end": v(-11.11, 1.64) * mm});
            skLineSegment(sketch, "E595", {"start": v(-11.11, 1.64) * mm, "end": v(-9.55, 0.44) * mm});
            skLineSegment(sketch, "E596", {"start": v(-9.55, 0.44) * mm, "end": v(-8.3, -0.65) * mm});
            skLineSegment(sketch, "E597", {"start": v(-8.3, -0.65) * mm, "end": v(-7.58, -1.24) * mm});
            skLineSegment(sketch, "E598", {"start": v(-7.58, -1.24) * mm, "end": v(-7.1, -0.95) * mm});
            skLineSegment(sketch, "E599", {"start": v(-7.1, -0.95) * mm, "end": v(-6.48, 0) * mm});
            skLineSegment(sketch, "E600", {"start": v(-6.48, 0) * mm, "end": v(-5.68, 1.72) * mm});
            skLineSegment(sketch, "E601", {"start": v(-5.68, 1.72) * mm, "end": v(-5.28, 3.17) * mm});
            skLineSegment(sketch, "E602", {"start": v(-5.28, 3.17) * mm, "end": v(-5.26, 4.43) * mm});
            skLineSegment(sketch, "E603", {"start": v(-12.62, 2.54) * mm, "end": v(-13, 3.03) * mm});
            skLineSegment(sketch, "E604", {"start": v(-13, 3.03) * mm, "end": v(-12.71, 3.47) * mm});
            skLineSegment(sketch, "E605", {"start": v(-12.71, 3.47) * mm, "end": v(-11.47, 3.63) * mm});
            skLineSegment(sketch, "E606", {"start": v(-11.47, 3.63) * mm, "end": v(-9.62, 3.85) * mm});
            skLineSegment(sketch, "E607", {"start": v(-9.62, 3.85) * mm, "end": v(-8.21, 4.16) * mm});
            skLineSegment(sketch, "E608", {"start": v(-8.21, 4.16) * mm, "end": v(-6.7, 4.35) * mm});
            skLineSegment(sketch, "E609", {"start": v(-6.7, 4.35) * mm, "end": v(-5.26, 4.43) * mm});
            skLineSegment(sketch, "E610", {"start": v(-3.19, 1.63) * mm, "end": v(-3.19, 2.54) * mm});
            skLineSegment(sketch, "E611", {"start": v(-3.19, 2.54) * mm, "end": v(-3.06, 3.6) * mm});
            skLineSegment(sketch, "E612", {"start": v(-3.06, 3.6) * mm, "end": v(-2.87, 4.26) * mm});
            skLineSegment(sketch, "E613", {"start": v(-2.87, 4.26) * mm, "end": v(-2.67, 4.94) * mm});
            skLineSegment(sketch, "E614", {"start": v(-2.67, 4.94) * mm, "end": v(-2.08, 6.06) * mm});
            skLineSegment(sketch, "E615", {"start": v(-2.08, 6.06) * mm, "end": v(-1.53, 5.47) * mm});
            skLineSegment(sketch, "E616", {"start": v(-1.53, 5.47) * mm, "end": v(-1.3, 4.83) * mm});
            skLineSegment(sketch, "E617", {"start": v(-1.3, 4.83) * mm, "end": v(-1.06, 4.03) * mm});
            skLineSegment(sketch, "E618", {"start": v(-1.06, 4.03) * mm, "end": v(-0.69, 3.13) * mm});
            skLineSegment(sketch, "E619", {"start": v(-0.69, 3.13) * mm, "end": v(-0.54, 2.43) * mm});
            skLineSegment(sketch, "E620", {"start": v(-0.54, 2.43) * mm, "end": v(-1.13, 2.02) * mm});
            skLineSegment(sketch, "E621", {"start": v(-1.13, 2.02) * mm, "end": v(-1.83, 1.84) * mm});
            skLineSegment(sketch, "E622", {"start": v(-1.83, 1.84) * mm, "end": v(-2.5, 1.7) * mm});
            skLineSegment(sketch, "E623", {"start": v(-2.5, 1.7) * mm, "end": v(-3.19, 1.63) * mm});
            skLineSegment(sketch, "E624", {"start": v(12.65, -2.45) * mm, "end": v(12.65, -2.9) * mm});
            skLineSegment(sketch, "E625", {"start": v(12.65, -2.9) * mm, "end": v(12.6, -5.13) * mm});
            skLineSegment(sketch, "E626", {"start": v(12.6, -5.13) * mm, "end": v(13.1, -5.1) * mm});
            skLineSegment(sketch, "E627", {"start": v(13.1, -5.1) * mm, "end": v(13.4, -4.78) * mm});
            skLineSegment(sketch, "E628", {"start": v(13.4, -4.78) * mm, "end": v(14.3, -3.64) * mm});
            skLineSegment(sketch, "E629", {"start": v(14.3, -3.64) * mm, "end": v(14.95, -2.94) * mm});
            skLineSegment(sketch, "E630", {"start": v(14.95, -2.94) * mm, "end": v(15.79, -1.7) * mm});
            skLineSegment(sketch, "E631", {"start": v(15.79, -1.7) * mm, "end": v(16.68, -0.34) * mm});
            skLineSegment(sketch, "E632", {"start": v(16.68, -0.34) * mm, "end": v(17.11, 0.37) * mm});
            skLineSegment(sketch, "E633", {"start": v(17.11, 0.37) * mm, "end": v(17.36, 0.7) * mm});
            skLineSegment(sketch, "E634", {"start": v(17.36, 0.7) * mm, "end": v(17.14, 1.23) * mm});
            skLineSegment(sketch, "E635", {"start": v(17.14, 1.23) * mm, "end": v(16.55, 1.23) * mm});
            skLineSegment(sketch, "E636", {"start": v(16.55, 1.23) * mm, "end": v(15.81, 1.23) * mm});
            skLineSegment(sketch, "E637", {"start": v(15.81, 1.23) * mm, "end": v(15.38, 0.77) * mm});
            skLineSegment(sketch, "E638", {"start": v(15.38, 0.77) * mm, "end": v(15.06, 0) * mm});
            skLineSegment(sketch, "E639", {"start": v(15.06, 0) * mm, "end": v(14.73, -0.6) * mm});
            skLineSegment(sketch, "E640", {"start": v(14.73, -0.6) * mm, "end": v(14.49, -1.56) * mm});
            skLineSegment(sketch, "E641", {"start": v(14.49, -1.56) * mm, "end": v(14.06, -1.99) * mm});
            skLineSegment(sketch, "E642", {"start": v(14.06, -1.99) * mm, "end": v(13.3, -2.2) * mm});
            skLineSegment(sketch, "E643", {"start": v(13.3, -2.2) * mm, "end": v(12.65, -2.45) * mm});
            skLineSegment(sketch, "E644", {"start": v(20.58, -2.8) * mm, "end": v(20.47, -3.2) * mm});
            skLineSegment(sketch, "E645", {"start": v(20.47, -3.2) * mm, "end": v(20.58, -3.48) * mm});
            skLineSegment(sketch, "E646", {"start": v(20.58, -3.48) * mm, "end": v(21.01, -3.53) * mm});
            skLineSegment(sketch, "E647", {"start": v(21.01, -3.53) * mm, "end": v(21.5, -3.26) * mm});
            skLineSegment(sketch, "E648", {"start": v(21.5, -3.26) * mm, "end": v(21.69, -2.8) * mm});
            skLineSegment(sketch, "E649", {"start": v(20.58, -2.8) * mm, "end": v(21.28, -2.53) * mm});
            skLineSegment(sketch, "E650", {"start": v(21.28, -2.53) * mm, "end": v(21.69, -2.8) * mm});
            skLineSegment(sketch, "E651", {"start": v(28.87, 1.46) * mm, "end": v(28.97, 3.14) * mm});
            skLineSegment(sketch, "E652", {"start": v(28.97, 3.14) * mm, "end": v(29.07, 4.53) * mm});
            skLineSegment(sketch, "E653", {"start": v(29.07, 4.53) * mm, "end": v(29.28, 5.11) * mm});
            skLineSegment(sketch, "E654", {"start": v(29.28, 5.11) * mm, "end": v(30.3, 4.53) * mm});
            skLineSegment(sketch, "E655", {"start": v(30.3, 4.53) * mm, "end": v(30.77, 3.41) * mm});
            skLineSegment(sketch, "E656", {"start": v(30.77, 3.41) * mm, "end": v(31.24, 2.36) * mm});
            skLineSegment(sketch, "E657", {"start": v(31.24, 2.36) * mm, "end": v(31.42, 1.46) * mm});
            skLineSegment(sketch, "E658", {"start": v(31.42, 1.46) * mm, "end": v(31.02, 1.15) * mm});
            skLineSegment(sketch, "E659", {"start": v(28.87, 1.46) * mm, "end": v(29.28, 1.15) * mm});
            skLineSegment(sketch, "E660", {"start": v(29.28, 1.15) * mm, "end": v(30.3, 1.15) * mm});
            skLineSegment(sketch, "E661", {"start": v(30.3, 1.15) * mm, "end": v(31.02, 1.15) * mm});
            skLineSegment(sketch, "E662", {"start": v(-8.33, -3.2) * mm, "end": v(-8.45, -4.07) * mm});
            skLineSegment(sketch, "E663", {"start": v(-8.45, -4.07) * mm, "end": v(-8.9, -4.76) * mm});
            skLineSegment(sketch, "E664", {"start": v(-8.9, -4.76) * mm, "end": v(-8.9, -5.5) * mm});
            skLineSegment(sketch, "E665", {"start": v(-8.9, -5.5) * mm, "end": v(-8.45, -6.07) * mm});
            skLineSegment(sketch, "E666", {"start": v(-8.45, -6.07) * mm, "end": v(-8, -6.6) * mm});
            skLineSegment(sketch, "E667", {"start": v(-8, -6.6) * mm, "end": v(-7.19, -6.6) * mm});
            skLineSegment(sketch, "E668", {"start": v(-7.19, -6.6) * mm, "end": v(-6.61, -6.27) * mm});
            skLineSegment(sketch, "E669", {"start": v(-6.61, -6.27) * mm, "end": v(-6.3, -5.73) * mm});
            skLineSegment(sketch, "E670", {"start": v(-6.3, -5.73) * mm, "end": v(-5.67, -5.09) * mm});
            skLineSegment(sketch, "E671", {"start": v(-5.67, -5.09) * mm, "end": v(-5.18, -5.17) * mm});
            skLineSegment(sketch, "E672", {"start": v(-5.18, -5.17) * mm, "end": v(-4.6, -5.8) * mm});
            skLineSegment(sketch, "E673", {"start": v(-4.6, -5.8) * mm, "end": v(-4, -6.27) * mm});
            skLineSegment(sketch, "E674", {"start": v(-4, -6.27) * mm, "end": v(-3.34, -6.27) * mm});
            skLineSegment(sketch, "E675", {"start": v(-3.34, -6.27) * mm, "end": v(-2.4, -6.27) * mm});
            skLineSegment(sketch, "E676", {"start": v(-2.4, -6.27) * mm, "end": v(-1.87, -5.82) * mm});
            skLineSegment(sketch, "E677", {"start": v(-1.87, -5.82) * mm, "end": v(-1.87, -5.17) * mm});
            skLineSegment(sketch, "E678", {"start": v(-1.87, -5.17) * mm, "end": v(-2.6, -4.6) * mm});
            skLineSegment(sketch, "E679", {"start": v(-2.6, -4.6) * mm, "end": v(-3.34, -4.15) * mm});
            skLineSegment(sketch, "E680", {"start": v(-3.34, -4.15) * mm, "end": v(-4, -3.53) * mm});
            skLineSegment(sketch, "E681", {"start": v(-4, -3.53) * mm, "end": v(-4.57, -3.29) * mm});
            skLineSegment(sketch, "E682", {"start": v(-4.57, -3.29) * mm, "end": v(-3.14, -1.53) * mm});
            skLineSegment(sketch, "E683", {"start": v(-3.14, -1.53) * mm, "end": v(-2.48, -0.8) * mm});
            skLineSegment(sketch, "E684", {"start": v(-2.48, -0.8) * mm, "end": v(-1.38, -0.35) * mm});
            skLineSegment(sketch, "E685", {"start": v(-1.38, -0.35) * mm, "end": v(0, 0) * mm});
            skLineSegment(sketch, "E686", {"start": v(0, 0) * mm, "end": v(0.62, -0.55) * mm});
            skLineSegment(sketch, "E687", {"start": v(0.62, -0.55) * mm, "end": v(0.92, -1.65) * mm});
            skLineSegment(sketch, "E688", {"start": v(0.92, -1.65) * mm, "end": v(1.2, -2.83) * mm});
            skLineSegment(sketch, "E689", {"start": v(1.2, -2.83) * mm, "end": v(1.69, -3.98) * mm});
            skLineSegment(sketch, "E690", {"start": v(1.69, -3.98) * mm, "end": v(2.26, -5.17) * mm});
            skLineSegment(sketch, "E691", {"start": v(2.26, -5.17) * mm, "end": v(2.41, -6.41) * mm});
            skLineSegment(sketch, "E692", {"start": v(2.41, -6.41) * mm, "end": v(2.78, -7.44) * mm});
            skLineSegment(sketch, "E693", {"start": v(2.78, -7.44) * mm, "end": v(3.82, -7.54) * mm});
            skLineSegment(sketch, "E694", {"start": v(3.82, -7.54) * mm, "end": v(4.5, -6.67) * mm});
            skLineSegment(sketch, "E695", {"start": v(4.5, -6.67) * mm, "end": v(4.75, -6.17) * mm});
            skLineSegment(sketch, "E696", {"start": v(4.75, -6.17) * mm, "end": v(4.84, -5.17) * mm});
            skLineSegment(sketch, "E697", {"start": v(4.84, -5.17) * mm, "end": v(4.88, -4.25) * mm});
            skLineSegment(sketch, "E698", {"start": v(4.88, -4.25) * mm, "end": v(5.21, -2.74) * mm});
            skLineSegment(sketch, "E699", {"start": v(5.21, -2.74) * mm, "end": v(5.47, -2.2) * mm});
            skLineSegment(sketch, "E700", {"start": v(5.47, -2.2) * mm, "end": v(5.45, -1.24) * mm});
            skLineSegment(sketch, "E701", {"start": v(5.45, -1.24) * mm, "end": v(5.85, -0.84) * mm});
            skLineSegment(sketch, "E702", {"start": v(5.85, -0.84) * mm, "end": v(6.19, -1) * mm});
            skLineSegment(sketch, "E703", {"start": v(6.19, -1) * mm, "end": v(6.43, -1.32) * mm});
            skLineSegment(sketch, "E704", {"start": v(6.43, -1.32) * mm, "end": v(6.43, -2.08) * mm});
            skLineSegment(sketch, "E705", {"start": v(6.43, -2.08) * mm, "end": v(6.65, -2.54) * mm});
            skLineSegment(sketch, "E706", {"start": v(6.65, -2.54) * mm, "end": v(6.67, -3.92) * mm});
            skLineSegment(sketch, "E707", {"start": v(6.67, -3.92) * mm, "end": v(6.67, -4.86) * mm});
            skLineSegment(sketch, "E708", {"start": v(6.67, -4.86) * mm, "end": v(6.73, -6.97) * mm});
            skLineSegment(sketch, "E709", {"start": v(6.73, -6.97) * mm, "end": v(6.94, -7.95) * mm});
            skLineSegment(sketch, "E710", {"start": v(6.94, -7.95) * mm, "end": v(7.72, -8.33) * mm});
            skLineSegment(sketch, "E711", {"start": v(7.72, -8.33) * mm, "end": v(8.5, -8.36) * mm});
            skLineSegment(sketch, "E712", {"start": v(8.5, -8.36) * mm, "end": v(8.94, -8.01) * mm});
            skLineSegment(sketch, "E713", {"start": v(8.94, -8.01) * mm, "end": v(9.1, -5.92) * mm});
            skLineSegment(sketch, "E714", {"start": v(9.1, -5.92) * mm, "end": v(10.07, -2.2) * mm});
            skLineSegment(sketch, "E715", {"start": v(10.07, -2.2) * mm, "end": v(10.35, -2.18) * mm});
            skLineSegment(sketch, "E716", {"start": v(10.35, -2.18) * mm, "end": v(10.6, -2.8) * mm});
            skLineSegment(sketch, "E717", {"start": v(10.6, -2.8) * mm, "end": v(10.6, -6.73) * mm});
            skLineSegment(sketch, "E718", {"start": v(10.6, -6.73) * mm, "end": v(10.74, -7.45) * mm});
            skLineSegment(sketch, "E719", {"start": v(10.74, -7.45) * mm, "end": v(10.9, -8.31) * mm});
            skLineSegment(sketch, "E720", {"start": v(10.9, -8.31) * mm, "end": v(11.07, -8.7) * mm});
            skLineSegment(sketch, "E721", {"start": v(11.07, -8.7) * mm, "end": v(11.65, -8.73) * mm});
            skLineSegment(sketch, "E722", {"start": v(11.65, -8.73) * mm, "end": v(12.2, -8.78) * mm});
            skLineSegment(sketch, "E723", {"start": v(12.2, -8.78) * mm, "end": v(12.54, -8.63) * mm});
            skLineSegment(sketch, "E724", {"start": v(12.54, -8.63) * mm, "end": v(12.78, -8.08) * mm});
            skLineSegment(sketch, "E725", {"start": v(12.78, -8.08) * mm, "end": v(12.93, -7.52) * mm});
            skLineSegment(sketch, "E726", {"start": v(12.93, -7.52) * mm, "end": v(13.3, -7.32) * mm});
            skLineSegment(sketch, "E727", {"start": v(13.3, -7.32) * mm, "end": v(14.73, -5.17) * mm});
            skLineSegment(sketch, "E728", {"start": v(14.73, -5.17) * mm, "end": v(15.81, -4.37) * mm});
            skLineSegment(sketch, "E729", {"start": v(15.81, -4.37) * mm, "end": v(16.52, -3.42) * mm});
            skLineSegment(sketch, "E730", {"start": v(16.52, -3.42) * mm, "end": v(17.25, -2.02) * mm});
            skLineSegment(sketch, "E731", {"start": v(17.25, -2.02) * mm, "end": v(17.68, -1.32) * mm});
            skLineSegment(sketch, "E732", {"start": v(17.68, -1.32) * mm, "end": v(18, -0.84) * mm});
            skLineSegment(sketch, "E733", {"start": v(18, -0.84) * mm, "end": v(18.66, -1.1) * mm});
            skLineSegment(sketch, "E734", {"start": v(18.66, -1.1) * mm, "end": v(18.68, -1.94) * mm});
            skLineSegment(sketch, "E735", {"start": v(18.68, -1.94) * mm, "end": v(18.5, -2.8) * mm});
            skLineSegment(sketch, "E736", {"start": v(18.5, -2.8) * mm, "end": v(18.22, -3.53) * mm});
            skLineSegment(sketch, "E737", {"start": v(18.22, -3.53) * mm, "end": v(18.17, -4.37) * mm});
            skLineSegment(sketch, "E738", {"start": v(18.17, -4.37) * mm, "end": v(17.77, -5.17) * mm});
            skLineSegment(sketch, "E739", {"start": v(17.77, -5.17) * mm, "end": v(17.47, -6.1) * mm});
            skLineSegment(sketch, "E740", {"start": v(17.47, -6.1) * mm, "end": v(17.44, -6.83) * mm});
            skLineSegment(sketch, "E741", {"start": v(17.44, -6.83) * mm, "end": v(17.98, -7.32) * mm});
            skLineSegment(sketch, "E742", {"start": v(17.98, -7.32) * mm, "end": v(18.74, -7.32) * mm});
            skLineSegment(sketch, "E743", {"start": v(18.74, -7.32) * mm, "end": v(19.3, -6.83) * mm});
            skLineSegment(sketch, "E744", {"start": v(19.3, -6.83) * mm, "end": v(19.74, -6.18) * mm});
            skLineSegment(sketch, "E745", {"start": v(19.74, -6.18) * mm, "end": v(24.96, -2.8) * mm});
            skLineSegment(sketch, "E746", {"start": v(24.96, -2.8) * mm, "end": v(25.61, -2.34) * mm});
            skLineSegment(sketch, "E747", {"start": v(25.61, -2.34) * mm, "end": v(25.8, -3.13) * mm});
            skLineSegment(sketch, "E748", {"start": v(25.8, -3.13) * mm, "end": v(25.66, -5.78) * mm});
            skLineSegment(sketch, "E749", {"start": v(25.66, -5.78) * mm, "end": v(25.53, -6.58) * mm});
            skLineSegment(sketch, "E750", {"start": v(25.53, -6.58) * mm, "end": v(25.12, -7.16) * mm});
            skLineSegment(sketch, "E751", {"start": v(25.12, -7.16) * mm, "end": v(25.06, -7.98) * mm});
            skLineSegment(sketch, "E752", {"start": v(25.06, -7.98) * mm, "end": v(25.8, -8.2) * mm});
            skLineSegment(sketch, "E753", {"start": v(25.8, -8.2) * mm, "end": v(26.7, -8.3) * mm});
            skLineSegment(sketch, "E754", {"start": v(26.7, -8.3) * mm, "end": v(26.89, -7.78) * mm});
            skLineSegment(sketch, "E755", {"start": v(26.89, -7.78) * mm, "end": v(27.18, -7.5) * mm});
            skLineSegment(sketch, "E756", {"start": v(27.18, -7.5) * mm, "end": v(27.27, -6.7) * mm});
            skLineSegment(sketch, "E757", {"start": v(27.27, -6.7) * mm, "end": v(27.32, -5.8) * mm});
            skLineSegment(sketch, "E758", {"start": v(27.32, -5.8) * mm, "end": v(27.48, -5.01) * mm});
            skLineSegment(sketch, "E759", {"start": v(27.48, -5.01) * mm, "end": v(27.8, -4.84) * mm});
            skLineSegment(sketch, "E760", {"start": v(27.8, -4.84) * mm, "end": v(28.34, -5.17) * mm});
            skLineSegment(sketch, "E761", {"start": v(28.34, -5.17) * mm, "end": v(28.78, -5.64) * mm});
            skLineSegment(sketch, "E762", {"start": v(28.78, -5.64) * mm, "end": v(29.28, -6.41) * mm});
            skLineSegment(sketch, "E763", {"start": v(29.28, -6.41) * mm, "end": v(29.83, -7.36) * mm});
            skLineSegment(sketch, "E764", {"start": v(29.83, -7.36) * mm, "end": v(30.27, -8.48) * mm});
            skLineSegment(sketch, "E765", {"start": v(30.27, -8.48) * mm, "end": v(30.54, -9.37) * mm});
            skLineSegment(sketch, "E766", {"start": v(30.54, -9.37) * mm, "end": v(30.7, -10.01) * mm});
            skLineSegment(sketch, "E767", {"start": v(30.7, -10.01) * mm, "end": v(31, -10.38) * mm});
            skLineSegment(sketch, "E768", {"start": v(31, -10.38) * mm, "end": v(31.73, -10.5) * mm});
            skLineSegment(sketch, "E769", {"start": v(31.73, -10.5) * mm, "end": v(32.16, -10.37) * mm});
            skLineSegment(sketch, "E770", {"start": v(32.16, -10.37) * mm, "end": v(32.45, -10.17) * mm});
            skLineSegment(sketch, "E771", {"start": v(32.45, -10.17) * mm, "end": v(32.57, -9.81) * mm});
            skLineSegment(sketch, "E772", {"start": v(32.57, -9.81) * mm, "end": v(32.4, -9.37) * mm});
            skLineSegment(sketch, "E773", {"start": v(32.4, -9.37) * mm, "end": v(32.34, -8.94) * mm});
            skLineSegment(sketch, "E774", {"start": v(32.34, -8.94) * mm, "end": v(32.25, -8.53) * mm});
            skLineSegment(sketch, "E775", {"start": v(32.25, -8.53) * mm, "end": v(32.1, -8.2) * mm});
            skLineSegment(sketch, "E776", {"start": v(32.1, -8.2) * mm, "end": v(31.75, -7.34) * mm});
            skLineSegment(sketch, "E777", {"start": v(31.75, -7.34) * mm, "end": v(30.6, -5.17) * mm});
            skLineSegment(sketch, "E778", {"start": v(30.6, -5.17) * mm, "end": v(29.42, -2.12) * mm});
            skLineSegment(sketch, "E779", {"start": v(29.42, -2.12) * mm, "end": v(29.28, -0.82) * mm});
            skLineSegment(sketch, "E780", {"start": v(29.28, -0.82) * mm, "end": v(30.02, -0.36) * mm});
            skLineSegment(sketch, "E781", {"start": v(30.02, -0.36) * mm, "end": v(33.28, -0.5) * mm});
            skLineSegment(sketch, "E782", {"start": v(33.28, -0.5) * mm, "end": v(33.92, -0.3) * mm});
            skLineSegment(sketch, "E783", {"start": v(33.92, -0.3) * mm, "end": v(34.11, 0.52) * mm});
            skLineSegment(sketch, "E784", {"start": v(34.11, 0.52) * mm, "end": v(33.92, 1.15) * mm});
            skLineSegment(sketch, "E785", {"start": v(33.92, 1.15) * mm, "end": v(32.42, 4.53) * mm});
            skLineSegment(sketch, "E786", {"start": v(32.42, 4.53) * mm, "end": v(30.54, 9.81) * mm});
            skLineSegment(sketch, "E787", {"start": v(30.54, 9.81) * mm, "end": v(30.07, 11.31) * mm});
            skLineSegment(sketch, "E788", {"start": v(30.07, 11.31) * mm, "end": v(29.28, 12.14) * mm});
            skLineSegment(sketch, "E789", {"start": v(29.28, 12.14) * mm, "end": v(28.67, 12.51) * mm});
            skLineSegment(sketch, "E790", {"start": v(28.67, 12.51) * mm, "end": v(27.37, 12.31) * mm});
            skLineSegment(sketch, "E791", {"start": v(27.37, 12.31) * mm, "end": v(26.87, 11.64) * mm});
            skLineSegment(sketch, "E792", {"start": v(26.87, 11.64) * mm, "end": v(26.92, 5.31) * mm});
            skLineSegment(sketch, "E793", {"start": v(26.92, 5.31) * mm, "end": v(26.84, 2.06) * mm});
            skLineSegment(sketch, "E794", {"start": v(26.84, 2.06) * mm, "end": v(26.4, 1.15) * mm});
            skLineSegment(sketch, "E795", {"start": v(26.4, 1.15) * mm, "end": v(26.37, 0) * mm});
            skLineSegment(sketch, "E796", {"start": v(26.37, 0) * mm, "end": v(24.28, -0.84) * mm});
            skLineSegment(sketch, "E797", {"start": v(24.28, -0.84) * mm, "end": v(22.96, -0.84) * mm});
            skLineSegment(sketch, "E798", {"start": v(22.96, -0.84) * mm, "end": v(21.82, -1.24) * mm});
            skLineSegment(sketch, "E799", {"start": v(21.82, -1.24) * mm, "end": v(20.97, -1.02) * mm});
            skLineSegment(sketch, "E800", {"start": v(20.97, -1.02) * mm, "end": v(21.04, -0.23) * mm});
            skLineSegment(sketch, "E801", {"start": v(21.04, -0.23) * mm, "end": v(21.5, 0.46) * mm});
            skLineSegment(sketch, "E802", {"start": v(21.5, 0.46) * mm, "end": v(21.57, 2.06) * mm});
            skLineSegment(sketch, "E803", {"start": v(21.57, 2.06) * mm, "end": v(22.26, 2.9) * mm});
            skLineSegment(sketch, "E804", {"start": v(22.26, 2.9) * mm, "end": v(23.24, 3.41) * mm});
            skLineSegment(sketch, "E805", {"start": v(23.24, 3.41) * mm, "end": v(24.18, 3.6) * mm});
            skLineSegment(sketch, "E806", {"start": v(24.18, 3.6) * mm, "end": v(25.03, 4.26) * mm});
            skLineSegment(sketch, "E807", {"start": v(25.03, 4.26) * mm, "end": v(24.81, 4.83) * mm});
            skLineSegment(sketch, "E808", {"start": v(24.81, 4.83) * mm, "end": v(24.28, 5.56) * mm});
            skLineSegment(sketch, "E809", {"start": v(24.28, 5.56) * mm, "end": v(23.59, 5.69) * mm});
            skLineSegment(sketch, "E810", {"start": v(23.59, 5.69) * mm, "end": v(22.58, 5.37) * mm});
            skLineSegment(sketch, "E811", {"start": v(22.58, 5.37) * mm, "end": v(21.63, 4.83) * mm});
            skLineSegment(sketch, "E812", {"start": v(21.63, 4.83) * mm, "end": v(21.5, 5.69) * mm});
            skLineSegment(sketch, "E813", {"start": v(21.5, 5.69) * mm, "end": v(21.65, 8.7) * mm});
            skLineSegment(sketch, "E814", {"start": v(21.65, 8.7) * mm, "end": v(21.86, 9.66) * mm});
            skLineSegment(sketch, "E815", {"start": v(21.86, 9.66) * mm, "end": v(22.73, 10.65) * mm});
            skLineSegment(sketch, "E816", {"start": v(22.73, 10.65) * mm, "end": v(23.59, 11.18) * mm});
            skLineSegment(sketch, "E817", {"start": v(23.59, 11.18) * mm, "end": v(24.81, 11.28) * mm});
            skLineSegment(sketch, "E818", {"start": v(24.81, 11.28) * mm, "end": v(25.67, 11.82) * mm});
            skLineSegment(sketch, "E819", {"start": v(25.67, 11.82) * mm, "end": v(25.8, 12.43) * mm});
            skLineSegment(sketch, "E820", {"start": v(25.8, 12.43) * mm, "end": v(25.28, 13.02) * mm});
            skLineSegment(sketch, "E821", {"start": v(25.28, 13.02) * mm, "end": v(24.81, 13.36) * mm});
            skLineSegment(sketch, "E822", {"start": v(24.81, 13.36) * mm, "end": v(24.18, 13.22) * mm});
            skLineSegment(sketch, "E823", {"start": v(24.18, 13.22) * mm, "end": v(23.59, 12.8) * mm});
            skLineSegment(sketch, "E824", {"start": v(23.59, 12.8) * mm, "end": v(22.89, 12.39) * mm});
            skLineSegment(sketch, "E825", {"start": v(22.89, 12.39) * mm, "end": v(22.3, 12.25) * mm});
            skLineSegment(sketch, "E826", {"start": v(22.3, 12.25) * mm, "end": v(21.5, 12.28) * mm});
            skLineSegment(sketch, "E827", {"start": v(21.5, 12.28) * mm, "end": v(20.95, 12.55) * mm});
            skLineSegment(sketch, "E828", {"start": v(20.95, 12.55) * mm, "end": v(20.47, 12.7) * mm});
            skLineSegment(sketch, "E829", {"start": v(20.47, 12.7) * mm, "end": v(20.03, 12.69) * mm});
            skLineSegment(sketch, "E830", {"start": v(20.03, 12.69) * mm, "end": v(19.66, 12.4) * mm});
            skLineSegment(sketch, "E831", {"start": v(19.66, 12.4) * mm, "end": v(19.25, 11.95) * mm});
            skLineSegment(sketch, "E832", {"start": v(19.25, 11.95) * mm, "end": v(19.06, 11.32) * mm});
            skLineSegment(sketch, "E833", {"start": v(19.06, 11.32) * mm, "end": v(19.06, 10.44) * mm});
            skLineSegment(sketch, "E834", {"start": v(19.06, 10.44) * mm, "end": v(19.06, 2.66) * mm});
            skLineSegment(sketch, "E835", {"start": v(19.06, 2.66) * mm, "end": v(18.68, 2.32) * mm});
            skLineSegment(sketch, "E836", {"start": v(18.68, 2.32) * mm, "end": v(18.26, 2.43) * mm});
            skLineSegment(sketch, "E837", {"start": v(18.26, 2.43) * mm, "end": v(15.08, 2.9) * mm});
            skLineSegment(sketch, "E838", {"start": v(15.08, 2.9) * mm, "end": v(14.47, 3.19) * mm});
            skLineSegment(sketch, "E839", {"start": v(14.47, 3.19) * mm, "end": v(14.1, 2.9) * mm});
            skLineSegment(sketch, "E840", {"start": v(14.1, 2.9) * mm, "end": v(13, -0.2) * mm});
            skLineSegment(sketch, "E841", {"start": v(13, -0.2) * mm, "end": v(12.86, -0.45) * mm});
            skLineSegment(sketch, "E842", {"start": v(12.86, -0.45) * mm, "end": v(12.86, 3.19) * mm});
            skLineSegment(sketch, "E843", {"start": v(12.86, 3.19) * mm, "end": v(12.96, 4.01) * mm});
            skLineSegment(sketch, "E844", {"start": v(12.96, 4.01) * mm, "end": v(13.12, 4.53) * mm});
            skLineSegment(sketch, "E845", {"start": v(13.12, 4.53) * mm, "end": v(13.41, 4.83) * mm});
            skLineSegment(sketch, "E846", {"start": v(13.41, 4.83) * mm, "end": v(13.38, 6.4) * mm});
            skLineSegment(sketch, "E847", {"start": v(13.38, 6.4) * mm, "end": v(13.48, 7.18) * mm});
            skLineSegment(sketch, "E848", {"start": v(13.48, 7.18) * mm, "end": v(13.83, 7.94) * mm});
            skLineSegment(sketch, "E849", {"start": v(13.83, 7.94) * mm, "end": v(14.47, 8.05) * mm});
            skLineSegment(sketch, "E850", {"start": v(14.47, 8.05) * mm, "end": v(14.91, 6.76) * mm});
            skLineSegment(sketch, "E851", {"start": v(14.91, 6.76) * mm, "end": v(15.06, 6.22) * mm});
            skLineSegment(sketch, "E852", {"start": v(15.06, 6.22) * mm, "end": v(15.81, 5.43) * mm});
            skLineSegment(sketch, "E853", {"start": v(15.81, 5.43) * mm, "end": v(16.81, 5.37) * mm});
            skLineSegment(sketch, "E854", {"start": v(16.81, 5.37) * mm, "end": v(17.36, 5.37) * mm});
            skLineSegment(sketch, "E855", {"start": v(17.36, 5.37) * mm, "end": v(17.62, 5.68) * mm});
            skLineSegment(sketch, "E856", {"start": v(17.62, 5.68) * mm, "end": v(17.77, 6.01) * mm});
            skLineSegment(sketch, "E857", {"start": v(17.77, 6.01) * mm, "end": v(17.77, 7.02) * mm});
            skLineSegment(sketch, "E858", {"start": v(17.77, 7.02) * mm, "end": v(17.47, 7.62) * mm});
            skLineSegment(sketch, "E859", {"start": v(17.47, 7.62) * mm, "end": v(17.35, 7.87) * mm});
            skLineSegment(sketch, "E860", {"start": v(17.35, 7.87) * mm, "end": v(15.8, 9.71) * mm});
            skLineSegment(sketch, "E861", {"start": v(15.8, 9.71) * mm, "end": v(14.58, 10.72) * mm});
            skLineSegment(sketch, "E862", {"start": v(14.58, 10.72) * mm, "end": v(14.1, 11.04) * mm});
            skLineSegment(sketch, "E863", {"start": v(14.1, 11.04) * mm, "end": v(12.78, 12.64) * mm});
            skLineSegment(sketch, "E864", {"start": v(12.78, 12.64) * mm, "end": v(12.2, 13) * mm});
            skLineSegment(sketch, "E865", {"start": v(12.2, 13) * mm, "end": v(11.53, 12.89) * mm});
            skLineSegment(sketch, "E866", {"start": v(11.53, 12.89) * mm, "end": v(11.23, 12.64) * mm});
            skLineSegment(sketch, "E867", {"start": v(11.23, 12.64) * mm, "end": v(11.05, 12.32) * mm});
            skLineSegment(sketch, "E868", {"start": v(11.05, 12.32) * mm, "end": v(11.05, 11.57) * mm});
            skLineSegment(sketch, "E869", {"start": v(11.05, 11.57) * mm, "end": v(11.23, 10.4) * mm});
            skLineSegment(sketch, "E870", {"start": v(11.23, 10.4) * mm, "end": v(11.23, 5.8) * mm});
            skLineSegment(sketch, "E871", {"start": v(11.23, 5.8) * mm, "end": v(11.23, 4.79) * mm});
            skLineSegment(sketch, "E872", {"start": v(11.23, 4.79) * mm, "end": v(10.9, 4.66) * mm});
            skLineSegment(sketch, "E873", {"start": v(10.9, 4.66) * mm, "end": v(10.52, 4.93) * mm});
            skLineSegment(sketch, "E874", {"start": v(10.52, 4.93) * mm, "end": v(9.92, 5.17) * mm});
            skLineSegment(sketch, "E875", {"start": v(9.92, 5.17) * mm, "end": v(9.4, 4.97) * mm});
            skLineSegment(sketch, "E876", {"start": v(9.4, 4.97) * mm, "end": v(9.07, 4.43) * mm});
            skLineSegment(sketch, "E877", {"start": v(9.07, 4.43) * mm, "end": v(9.03, 2.86) * mm});
            skLineSegment(sketch, "E878", {"start": v(9.03, 2.86) * mm, "end": v(8.68, 2.15) * mm});
            skLineSegment(sketch, "E879", {"start": v(8.68, 2.15) * mm, "end": v(8.48, 1.78) * mm});
            skLineSegment(sketch, "E880", {"start": v(8.48, 1.78) * mm, "end": v(8.05, 1.69) * mm});
            skLineSegment(sketch, "E881", {"start": v(8.05, 1.69) * mm, "end": v(7.89, 2.93) * mm});
            skLineSegment(sketch, "E882", {"start": v(7.89, 2.93) * mm, "end": v(7.66, 4.31) * mm});
            skLineSegment(sketch, "E883", {"start": v(7.66, 4.31) * mm, "end": v(7.28, 6.17) * mm});
            skLineSegment(sketch, "E884", {"start": v(7.28, 6.17) * mm, "end": v(7.02, 8.07) * mm});
            skLineSegment(sketch, "E885", {"start": v(7.02, 8.07) * mm, "end": v(7.04, 9.77) * mm});
            skLineSegment(sketch, "E886", {"start": v(7.04, 9.77) * mm, "end": v(6.5, 11.06) * mm});
            skLineSegment(sketch, "E887", {"start": v(6.5, 11.06) * mm, "end": v(5.75, 11.63) * mm});
            skLineSegment(sketch, "E888", {"start": v(5.75, 11.63) * mm, "end": v(4.88, 11.52) * mm});
            skLineSegment(sketch, "E889", {"start": v(4.88, 11.52) * mm, "end": v(4.77, 9.44) * mm});
            skLineSegment(sketch, "E890", {"start": v(4.77, 9.44) * mm, "end": v(4.81, 5) * mm});
            skLineSegment(sketch, "E891", {"start": v(4.81, 5) * mm, "end": v(4.57, 4.18) * mm});
            skLineSegment(sketch, "E892", {"start": v(4.57, 4.18) * mm, "end": v(4.42, 3.72) * mm});
            skLineSegment(sketch, "E893", {"start": v(4.42, 3.72) * mm, "end": v(4.3, 2.1) * mm});
            skLineSegment(sketch, "E894", {"start": v(4.3, 2.1) * mm, "end": v(4.22, 0.88) * mm});
            skLineSegment(sketch, "E895", {"start": v(4.22, 0.88) * mm, "end": v(3.48, -0.84) * mm});
            skLineSegment(sketch, "E896", {"start": v(3.48, -0.84) * mm, "end": v(3.13, -1.21) * mm});
            skLineSegment(sketch, "E897", {"start": v(3.13, -1.21) * mm, "end": v(2.74, -0.84) * mm});
            skLineSegment(sketch, "E898", {"start": v(2.74, -0.84) * mm, "end": v(2.43, 0) * mm});
            skLineSegment(sketch, "E899", {"start": v(2.43, 0) * mm, "end": v(2.4, 0.64) * mm});
            skLineSegment(sketch, "E900", {"start": v(2.4, 0.64) * mm, "end": v(2.82, 1.34) * mm});
            skLineSegment(sketch, "E901", {"start": v(2.82, 1.34) * mm, "end": v(3.1, 1.82) * mm});
            skLineSegment(sketch, "E902", {"start": v(3.1, 1.82) * mm, "end": v(3.02, 2.56) * mm});
            skLineSegment(sketch, "E903", {"start": v(3.02, 2.56) * mm, "end": v(2.45, 2.93) * mm});
            skLineSegment(sketch, "E904", {"start": v(2.45, 2.93) * mm, "end": v(1.67, 2.93) * mm});
            skLineSegment(sketch, "E905", {"start": v(1.67, 2.93) * mm, "end": v(1.32, 3.83) * mm});
            skLineSegment(sketch, "E906", {"start": v(1.32, 3.83) * mm, "end": v(0.95, 5.23) * mm});
            skLineSegment(sketch, "E907", {"start": v(0.95, 5.23) * mm, "end": v(0.53, 6.7) * mm});
            skLineSegment(sketch, "E908", {"start": v(0.53, 6.7) * mm, "end": v(0.4, 7.78) * mm});
            skLineSegment(sketch, "E909", {"start": v(0.4, 7.78) * mm, "end": v(0.49, 8.94) * mm});
            skLineSegment(sketch, "E910", {"start": v(0.49, 8.94) * mm, "end": v(0.33, 10.6) * mm});
            skLineSegment(sketch, "E911", {"start": v(0.33, 10.6) * mm, "end": v(0.3, 12.66) * mm});
            skLineSegment(sketch, "E912", {"start": v(0.3, 12.66) * mm, "end": v(0, 13.09) * mm});
            skLineSegment(sketch, "E913", {"start": v(0, 13.09) * mm, "end": v(-0.8, 13.31) * mm});
            skLineSegment(sketch, "E914", {"start": v(-0.8, 13.31) * mm, "end": v(-1.34, 13.17) * mm});
            skLineSegment(sketch, "E915", {"start": v(-1.34, 13.17) * mm, "end": v(-2.08, 11.97) * mm});
            skLineSegment(sketch, "E916", {"start": v(-2.08, 11.97) * mm, "end": v(-2.9, 9.65) * mm});
            skLineSegment(sketch, "E917", {"start": v(-2.9, 9.65) * mm, "end": v(-3.38, 8.19) * mm});
            skLineSegment(sketch, "E918", {"start": v(-3.38, 8.19) * mm, "end": v(-3.95, 7.37) * mm});
            skLineSegment(sketch, "E919", {"start": v(-3.95, 7.37) * mm, "end": v(-4.64, 7.17) * mm});
            skLineSegment(sketch, "E920", {"start": v(-4.64, 7.17) * mm, "end": v(-5.25, 7.9) * mm});
            skLineSegment(sketch, "E921", {"start": v(-5.25, 7.9) * mm, "end": v(-6.47, 8.72) * mm});
            skLineSegment(sketch, "E922", {"start": v(-6.47, 8.72) * mm, "end": v(-7.9, 9.65) * mm});
            skLineSegment(sketch, "E923", {"start": v(-7.9, 9.65) * mm, "end": v(-9, 10.22) * mm});
            skLineSegment(sketch, "E924", {"start": v(-9, 10.22) * mm, "end": v(-10.22, 10.63) * mm});
            skLineSegment(sketch, "E925", {"start": v(-10.22, 10.63) * mm, "end": v(-11.03, 11.48) * mm});
            skLineSegment(sketch, "E926", {"start": v(-11.03, 11.48) * mm, "end": v(-11.84, 12.14) * mm});
            skLineSegment(sketch, "E927", {"start": v(-11.84, 12.14) * mm, "end": v(-12.8, 13.17) * mm});
            skLineSegment(sketch, "E928", {"start": v(-12.8, 13.17) * mm, "end": v(-15.2, 13.17) * mm});
            skLineSegment(sketch, "E929", {"start": v(-15.2, 13.17) * mm, "end": v(-15.5, 11.73) * mm});
            skLineSegment(sketch, "E930", {"start": v(-15.2, 13.17) * mm, "end": v(-15.2, 13.17) * mm});
            skLineSegment(sketch, "E931", {"start": v(-15.5, 11.73) * mm, "end": v(-15.06, 10.43) * mm});
            skLineSegment(sketch, "E932", {"start": v(-15.06, 10.43) * mm, "end": v(-15.02, 9.4) * mm});
            skLineSegment(sketch, "E933", {"start": v(-15.02, 9.4) * mm, "end": v(-15.59, 8.72) * mm});
            skLineSegment(sketch, "E934", {"start": v(-15.59, 8.72) * mm, "end": v(-16.6, 8.4) * mm});
            skLineSegment(sketch, "E935", {"start": v(-16.6, 8.4) * mm, "end": v(-17.3, 8.68) * mm});
            skLineSegment(sketch, "E936", {"start": v(-17.3, 8.68) * mm, "end": v(-17.3, 9.73) * mm});
            skLineSegment(sketch, "E937", {"start": v(-17.3, 9.73) * mm, "end": v(-16.97, 11.77) * mm});
            skLineSegment(sketch, "E938", {"start": v(-16.97, 11.77) * mm, "end": v(-16.97, 12.75) * mm});
            skLineSegment(sketch, "E939", {"start": v(-16.97, 12.75) * mm, "end": v(-17.3, 13.52) * mm});
            skLineSegment(sketch, "E940", {"start": v(-17.3, 13.52) * mm, "end": v(-18.27, 13.4) * mm});
            skLineSegment(sketch, "E941", {"start": v(-18.27, 13.4) * mm, "end": v(-18.88, 12.75) * mm});
            skLineSegment(sketch, "E942", {"start": v(-18.88, 12.75) * mm, "end": v(-19.74, 12.75) * mm});
            skLineSegment(sketch, "E943", {"start": v(-19.74, 12.75) * mm, "end": v(-21.12, 12.34) * mm});
            skLineSegment(sketch, "E944", {"start": v(-21.12, 12.34) * mm, "end": v(-29.02, 7.98) * mm});
            skLineSegment(sketch, "E945", {"start": v(-29.02, 7.98) * mm, "end": v(-30.44, 7.37) * mm});
            skLineSegment(sketch, "E946", {"start": v(-30.44, 7.37) * mm, "end": v(-32.1, 6.64) * mm});
            skLineSegment(sketch, "E947", {"start": v(-32.1, 6.64) * mm, "end": v(-33.04, 6.07) * mm});
            skLineSegment(sketch, "E948", {"start": v(-33.04, 6.07) * mm, "end": v(-33.78, 5.42) * mm});
            skLineSegment(sketch, "E949", {"start": v(-33.78, 5.42) * mm, "end": v(-33.98, 4.49) * mm});
            skLineSegment(sketch, "E950", {"start": v(-33.98, 4.49) * mm, "end": v(-33.61, 3.26) * mm});
            skLineSegment(sketch, "E951", {"start": v(-33.61, 3.26) * mm, "end": v(-32.1, 2.53) * mm});
            skLineSegment(sketch, "E952", {"start": v(-32.1, 2.53) * mm, "end": v(-30.77, 2.17) * mm});
            skLineSegment(sketch, "E953", {"start": v(-30.77, 2.17) * mm, "end": v(-27.18, 0.86) * mm});
            skLineSegment(sketch, "E954", {"start": v(-27.18, 0.86) * mm, "end": v(-26.09, 0.66) * mm});
            skLineSegment(sketch, "E955", {"start": v(-26.09, 0.66) * mm, "end": v(-25.23, 0) * mm});
            skLineSegment(sketch, "E956", {"start": v(-25.23, 0) * mm, "end": v(-25.23, -0.76) * mm});
            skLineSegment(sketch, "E957", {"start": v(-25.23, -0.76) * mm, "end": v(-27.3, -1.74) * mm});
            skLineSegment(sketch, "E958", {"start": v(-27.3, -1.74) * mm, "end": v(-28.12, -2.19) * mm});
            skLineSegment(sketch, "E959", {"start": v(-28.12, -2.19) * mm, "end": v(-28.98, -2.31) * mm});
            skLineSegment(sketch, "E960", {"start": v(-28.98, -2.31) * mm, "end": v(-30.03, -2.76) * mm});
            skLineSegment(sketch, "E961", {"start": v(-16.52, 3.56) * mm, "end": v(-17.52, 3.73) * mm});
            skLineSegment(sketch, "E962", {"start": v(-8.85, 7.8) * mm, "end": v(-9.8, 8.25) * mm});
            skLineSegment(sketch, "E963", {"start": v(-9.8, 8.25) * mm, "end": v(-11.4, 8.25) * mm});
            skLineSegment(sketch, "E964", {"start": v(-11.95, 7.33) * mm, "end": v(-11.4, 8.25) * mm});
            skSolve(sketch);
        }
        {
            var Q0;
            Q0 = qSketchRegion(id + "F0", true);
            extrude(context, id + "F1", {"entities" : qUnion([Q0]), "depth" : 6.35 * mm});
        }
    });
